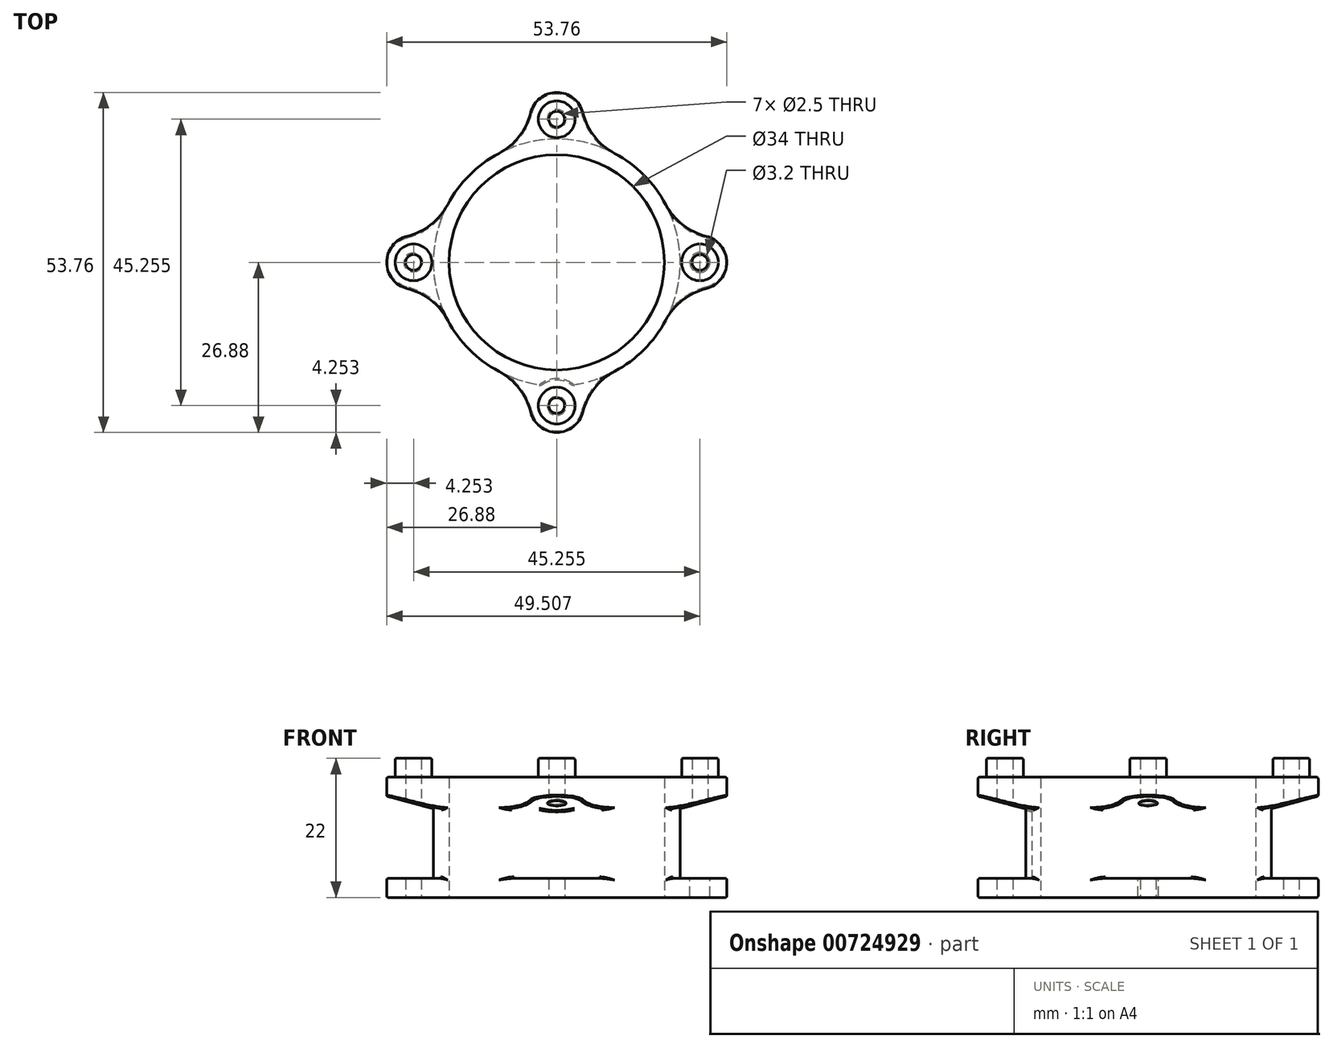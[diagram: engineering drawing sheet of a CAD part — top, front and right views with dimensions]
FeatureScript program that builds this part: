
annotation { "Feature Type Name" : "Feature", "Feature Type Description" : "" }
export const myFeature = defineFeature(function(context is Context, id is Id, definition is map)
    precondition{}
    {
        {
            var Q0;
            Q0=qCreatedBy(makeId("Top.planeOp"),FACE);
            var sketch = newSketch(context, id + "F0", { "sketchPlane" : qUnion([Q0])});
            skCircle(sketch, "E0", {"center": v(0, 0) * mm, "radius": 17 * mm});
            skArc(sketch, "E1", {"start": v(17.22, 9.14) * mm, "mid": v(13.79, 13.79) * mm, "end": v(9.14, 17.22) * mm});
            skCircle(sketch, "E2", {"center": v(22.63, 0) * mm, "radius": 1.25 * mm});
            skLineSegment(sketch, "E3.bottom", {"start": v(0, 0) * mm, "end": v(22.63, 0) * mm, "construction": true});
            skLineSegment(sketch, "E3.top", {"start": v(0, -22.63) * mm, "end": v(22.63, -22.63) * mm, "construction": true});
            skLineSegment(sketch, "E3.left", {"start": v(0, 0) * mm, "end": v(0, -22.63) * mm, "construction": true});
            skLineSegment(sketch, "E3.right", {"start": v(22.63, 0) * mm, "end": v(22.63, -22.63) * mm, "construction": true});
            skArc(sketch, "E4", {"start": v(23.65, -4.13) * mm, "mid": v(26.88, 0) * mm, "end": v(23.65, 4.13) * mm});
            skPoint(sketch, "E5.visualSharp", {"position": v(19.32, 2.67) * mm});
            skArc(sketch, "E5.filletArc", {"start": v(17.22, 9.14) * mm, "mid": v(19.9, 5.95) * mm, "end": v(23.65, 4.13) * mm});
            skPoint(sketch, "E6.visualSharp", {"position": v(19.32, -2.67) * mm});
            skArc(sketch, "E6.filletArc", {"start": v(23.65, -4.13) * mm, "mid": v(19.9, -5.95) * mm, "end": v(17.22, -9.14) * mm});
            skArc(sketch, "E7.1.0", {"start": v(-9.14, 17.22) * mm, "mid": v(-5.95, 19.9) * mm, "end": v(-4.13, 23.65) * mm});
            skArc(sketch, "E7.1.1", {"start": v(4.13, 23.65) * mm, "mid": v(0, 26.88) * mm, "end": v(-4.13, 23.65) * mm});
            skArc(sketch, "E7.1.2", {"start": v(4.13, 23.65) * mm, "mid": v(5.95, 19.9) * mm, "end": v(9.14, 17.22) * mm});
            skCircle(sketch, "E7.1.3", {"center": v(0, 22.63) * mm, "radius": 1.25 * mm});
            skArc(sketch, "E7.2.0", {"start": v(-17.22, -9.14) * mm, "mid": v(-19.9, -5.95) * mm, "end": v(-23.65, -4.13) * mm});
            skArc(sketch, "E7.2.1", {"start": v(-23.65, 4.13) * mm, "mid": v(-26.88, 0) * mm, "end": v(-23.65, -4.13) * mm});
            skArc(sketch, "E7.2.2", {"start": v(-23.65, 4.13) * mm, "mid": v(-19.9, 5.95) * mm, "end": v(-17.22, 9.14) * mm});
            skCircle(sketch, "E7.2.3", {"center": v(-22.63, 0) * mm, "radius": 1.25 * mm});
            skArc(sketch, "E8.trimOffspring", {"start": v(-9.14, 17.22) * mm, "mid": v(-13.79, 13.79) * mm, "end": v(-17.22, 9.14) * mm});
            skArc(sketch, "E9.trimOffspring", {"start": v(9.14, -17.22) * mm, "mid": v(13.79, -13.79) * mm, "end": v(17.22, -9.14) * mm});
            skArc(sketch, "E10.4.3.0", {"start": v(-4.13, -23.65) * mm, "mid": v(0, -26.88) * mm, "end": v(4.13, -23.65) * mm});
            skArc(sketch, "E10.8.3.0", {"start": v(-4.13, -23.65) * mm, "mid": v(-5.95, -19.9) * mm, "end": v(-9.14, -17.22) * mm});
            skArc(sketch, "E10.11.3.0", {"start": v(9.14, -17.22) * mm, "mid": v(5.95, -19.9) * mm, "end": v(4.13, -23.65) * mm});
            skCircle(sketch, "E10.12.3.0", {"center": v(0, -22.63) * mm, "radius": 1.25 * mm});
            skArc(sketch, "E11.trimOffspring", {"start": v(-17.22, -9.14) * mm, "mid": v(-13.79, -13.79) * mm, "end": v(-9.14, -17.22) * mm});
            skSolve(sketch);
        }
        {
            var Q0;
            Q0=makeQuery(id+"F0.imprint","IMPRINT",FACE,{"disambiguationData":[TD([[makeQuery(id+"F0.imprint","IMPRINT",EDGE,{"derivedFrom":sQuery(id+"F0.wireOp",EDGE,"E0")}),-1.0]])]});
            extrude(context, id + "F1", {"entities" : qUnion([Q0]), "depth" : 22 * mm, "offsetDistance" : 25 * mm});
        }
        {
            var Q0;
            Q0=qCreatedBy(makeId("Front.planeOp"),FACE);
            var sketch = newSketch(context, id + "F2", { "sketchPlane" : qUnion([Q0])});
            skLineSegment(sketch, "E12.bottom", {"start": v(-26.88, 16) * mm, "end": v(-19.5, 14.02) * mm});
            skLineSegment(sketch, "E12.top", {"start": v(-26.88, 3) * mm, "end": v(-19.5, 3) * mm});
            skLineSegment(sketch, "E12.left", {"start": v(-26.88, 16) * mm, "end": v(-26.88, 3) * mm});
            skLineSegment(sketch, "E12.right", {"start": v(-19.5, 14.02) * mm, "end": v(-19.5, 3) * mm});
            skLineSegment(sketch, "E13", {"start": v(-26.88, 0) * mm, "end": v(-26.88, 22) * mm});
            skLineSegment(sketch, "E14", {"start": v(-17, 0) * mm, "end": v(-17, 22) * mm, "construction": true});
            skSolve(sketch);
        }
        {
            var Q0;
            Q0 = qSketchRegion(id + "F2", true);
            var Q1;
            Q1=makeQuery(id+"F1.opExtrude","SWEPT_FACE",FACE,{"disambiguationData":[OSD([sQuery(id+"F0.wireOp",EDGE,"E0")])]});
            revolve(context, id + "F3", {"operationType" : NewBodyOperationType.REMOVE, "surfaceOperationType" : NewSurfaceOperationType.NEW, "entities" : qUnion([Q0]), "axis" : qUnion([Q1]), "revolveType" : RevolveType.FULL, "oppositeDirection" : true});
        }
        {
            var Q0;
            Q0=makeQuery(id+"F3.boolean.opBoolean","COPY",FACE,{"disambiguationData":[TD([makeQuery(id+"F1.opExtrude","SWEPT_FACE",FACE,{"disambiguationData":[OSD([sQuery(id+"F0.wireOp",EDGE,"E10.4.3.0")])]})])],"derivedFrom":makeQuery(id+"F3.opRevolve","SWEPT_FACE",FACE,{"disambiguationData":[OSD([sQuery(id+"F2.wireOp",EDGE,"E12.top")])]})});
            var sketch = newSketch(context, id + "F4", { "sketchPlane" : qUnion([Q0])});
            skCircle(sketch, "E15", {"center": v(0, -22.63) * mm, "radius": 4.25 * mm});
            skSolve(sketch);
        }
        {
            var Q0;
            Q0 = qSketchRegion(id + "F4", true);
            var Q1;
            Q1=makeQuery(id+"F3.boolean.opBoolean","COPY",FACE,{"disambiguationData":[TD([makeQuery(id+"F1.opExtrude","SWEPT_FACE",FACE,{"disambiguationData":[OSD([sQuery(id+"F0.wireOp",EDGE,"E10.4.3.0")])]})])],"derivedFrom":makeQuery(id+"F3.opRevolve","SWEPT_FACE",FACE,{"disambiguationData":[OSD([sQuery(id+"F2.wireOp",EDGE,"E12.bottom")])]})});
            extrude(context, id + "F5", {"entities" : qUnion([Q0]), "operationType" : NewBodyOperationType.REMOVE, "endBound" : BoundingType.UP_TO_SURFACE, "depth" : 10 * mm, "endBoundEntityFace" : qUnion([Q1]), "offsetDistance" : 25 * mm});
        }
        {
            var Q0;
            Q0=makeQuery(id+"F1.opExtrude","CAP_FACE",FACE,{"disambiguationData":[OSD([sQuery(id+"F0.wireOp",EDGE,"E0"),sQuery(id+"F0.wireOp",EDGE,"E1"),sQuery(id+"F0.wireOp",EDGE,"E2"),sQuery(id+"F0.wireOp",EDGE,"E4"),sQuery(id+"F0.wireOp",EDGE,"E5.filletArc"),sQuery(id+"F0.wireOp",EDGE,"E6.filletArc"),sQuery(id+"F0.wireOp",EDGE,"E7.1.0"),sQuery(id+"F0.wireOp",EDGE,"E7.1.1"),sQuery(id+"F0.wireOp",EDGE,"E7.1.2"),sQuery(id+"F0.wireOp",EDGE,"E7.1.3"),sQuery(id+"F0.wireOp",EDGE,"E7.2.0"),sQuery(id+"F0.wireOp",EDGE,"E7.2.1"),sQuery(id+"F0.wireOp",EDGE,"E7.2.2"),sQuery(id+"F0.wireOp",EDGE,"E7.2.3"),sQuery(id+"F0.wireOp",EDGE,"E8.trimOffspring"),sQuery(id+"F0.wireOp",EDGE,"E9.trimOffspring"),sQuery(id+"F0.wireOp",EDGE,"E10.4.3.0"),sQuery(id+"F0.wireOp",EDGE,"E10.8.3.0"),sQuery(id+"F0.wireOp",EDGE,"E10.11.3.0"),sQuery(id+"F0.wireOp",EDGE,"E10.12.3.0"),sQuery(id+"F0.wireOp",EDGE,"E11.trimOffspring")])],"isStart":false});
            var sketch = newSketch(context, id + "F6", { "sketchPlane" : qUnion([Q0])});
            skCircle(sketch, "E16", {"center": v(22.63, 0) * mm, "radius": 2.9 * mm});
            skCircle(sketch, "E17.1.0", {"center": v(0, 22.63) * mm, "radius": 2.9 * mm});
            skCircle(sketch, "E17.2.0", {"center": v(-22.63, 0) * mm, "radius": 2.9 * mm});
            skCircle(sketch, "E17.3.0", {"center": v(0, -22.63) * mm, "radius": 2.9 * mm});
            skPoint(sketch, "E17.center", {"position": v(0, 0) * mm});
            skCircle(sketch, "E18", {"center": v(0, 0) * mm, "radius": 46.42 * mm});
            skSolve(sketch);
        }
        {
            var Q0;
            Q0 = qSketchRegion(id + "F6", true);
            extrude(context, id + "F7", {"entities" : qUnion([Q0]), "operationType" : NewBodyOperationType.REMOVE, "oppositeDirection" : true, "depth" : 3 * mm, "offsetDistance" : 25 * mm});
        }
        {
            var Q0;
            Q0=makeQuery(id+"FENhaPdsYRhXpVq_1.1.F5.boolean.opBoolean","MERGE",FACE,{"derivedFrom":[makeQuery(id+"F3.boolean.opBoolean","COPY",FACE,{"disambiguationData":[TD([makeQuery(id+"F1.opExtrude","SWEPT_FACE",FACE,{"disambiguationData":[OSD([sQuery(id+"F0.wireOp",EDGE,"E2")])]})])],"derivedFrom":makeQuery(id+"F3.opRevolve","SWEPT_FACE",FACE,{"disambiguationData":[OSD([sQuery(id+"F2.wireOp",EDGE,"E12.top")])]})}),makeQuery(id+"FENhaPdsYRhXpVq_1.1.F5.opExtrude","CAP_FACE",FACE,{"disambiguationData":[OSD([sQuery(id+"F4.wireOp",EDGE,"E15")])],"isStart":true})]});
            var sketch = newSketch(context, id + "F8", { "sketchPlane" : qUnion([Q0])});
            skPoint(sketch, "E19", {"position": v(22.63, 0) * mm});
            skSolve(sketch);
        }
        {
            var Q0;
            Q0=sQuery(id+"F8.wireOp",VERTEX,"E19");
            var Q1;
            Q1=makeQuery(id+"F1.opExtrude","SWEPT_BODY",BODY,{"disambiguationData":[OSD([sQuery(id+"F0.wireOp",EDGE,"E0"),sQuery(id+"F0.wireOp",EDGE,"E1"),sQuery(id+"F0.wireOp",EDGE,"E2"),sQuery(id+"F0.wireOp",EDGE,"E4"),sQuery(id+"F0.wireOp",EDGE,"E5.filletArc"),sQuery(id+"F0.wireOp",EDGE,"E6.filletArc"),sQuery(id+"F0.wireOp",EDGE,"E7.1.0"),sQuery(id+"F0.wireOp",EDGE,"E7.1.1"),sQuery(id+"F0.wireOp",EDGE,"E7.1.2"),sQuery(id+"F0.wireOp",EDGE,"E7.1.3"),sQuery(id+"F0.wireOp",EDGE,"E7.2.0"),sQuery(id+"F0.wireOp",EDGE,"E7.2.1"),sQuery(id+"F0.wireOp",EDGE,"E7.2.2"),sQuery(id+"F0.wireOp",EDGE,"E7.2.3"),sQuery(id+"F0.wireOp",EDGE,"E8.trimOffspring"),sQuery(id+"F0.wireOp",EDGE,"E9.trimOffspring"),sQuery(id+"F0.wireOp",EDGE,"E10.4.3.0"),sQuery(id+"F0.wireOp",EDGE,"E10.8.3.0"),sQuery(id+"F0.wireOp",EDGE,"E10.11.3.0"),sQuery(id+"F0.wireOp",EDGE,"E10.12.3.0"),sQuery(id+"F0.wireOp",EDGE,"E11.trimOffspring")])]});
            hole(context, id + "F9", {"style" : HoleStyle.SIMPLE, "endStyle" : HoleEndStyle.THROUGH, "holeDiameter" : 3.2 * mm, "majorDiameter" : 5 * mm, "isTappedThrough" : true, "tappedDepth" : 12 * mm, "tapClearance" : 3, "locations" : qUnion([Q0]), "scope" : qUnion([Q1])});
        }
        {
            var Q0;
            Q0=makeQuery(id+"F1.opExtrude","CAP_EDGE",EDGE,{"disambiguationData":[OSD([sQuery(id+"F0.wireOp",EDGE,"E7.2.0")])],"isStart":true});
            var Q1;
            {var subQ1=sQuery(id+"F0.wireOp",EDGE,"E9.trimOffspring");var subQ2=makeQuery(id+"F1.opExtrude","SWEPT_FACE",FACE,{"disambiguationData":[OSD([subQ1])]});var subQ3=sQuery(id+"F0.wireOp",EDGE,"E8.trimOffspring");var subQ4=makeQuery(id+"F1.opExtrude","SWEPT_FACE",FACE,{"disambiguationData":[OSD([subQ3])]});var subQ7=sQuery(id+"F0.wireOp",EDGE,"E1");var subQ8=makeQuery(id+"F1.opExtrude","SWEPT_FACE",FACE,{"disambiguationData":[OSD([subQ7])]});var subQ9=makeQuery(id+"F3.opRevolve","SWEPT_FACE",FACE,{"disambiguationData":[OSD([sQuery(id+"F2.wireOp",EDGE,"E12.right")])]});var subQ16=sQuery(id+"F0.wireOp",EDGE,"E11.trimOffspring");var subQ17=makeQuery(id+"F1.opExtrude","SWEPT_FACE",FACE,{"disambiguationData":[OSD([subQ16])]});var subQ25=sQuery(id+"F0.wireOp",EDGE,"E6.filletArc");var subQ26=makeQuery(id+"F1.opExtrude","SWEPT_FACE",FACE,{"disambiguationData":[OSD([subQ25])]});Q1=makeQuery(id+"FENhaPdsYRhXpVq_1.1.F5.boolean.opBoolean","SPLIT",FACE,{"disambiguationData":[TD([subQ26])],"derivedFrom":makeQuery(id+"F3.boolean.opBoolean","MERGE",FACE,{"derivedFrom":[subQ8,subQ4,subQ2,subQ17,subQ9]})});}
            var Q2;
            Q2=makeQuery(id+"F1.opExtrude","CAP_EDGE",EDGE,{"disambiguationData":[OSD([sQuery(id+"F0.wireOp",EDGE,"E0")])],"isStart":false});
            var Q3;
            Q3=makeQuery(id+"F1.opExtrude","CAP_EDGE",EDGE,{"disambiguationData":[OSD([sQuery(id+"F0.wireOp",EDGE,"E10.11.3.0")])],"isStart":true});
            var Q4;
            Q4=makeQuery(id+"F3.boolean.opBoolean","INTERSECT",EDGE,{"derivedFrom":[makeQuery(id+"F1.opExtrude","SWEPT_FACE",FACE,{"disambiguationData":[OSD([sQuery(id+"F0.wireOp",EDGE,"E10.4.3.0")])]}),makeQuery(id+"F3.opRevolve","SWEPT_FACE",FACE,{"disambiguationData":[OSD([sQuery(id+"F2.wireOp",EDGE,"E12.top")])]})]});
            var Q5;
            Q5=makeQuery(id+"F1.opExtrude","CAP_EDGE",EDGE,{"disambiguationData":[OSD([sQuery(id+"F0.wireOp",EDGE,"E7.2.1")])],"isStart":true});
            var Q6;
            {var subQ1=sQuery(id+"F0.wireOp",EDGE,"E7.2.1");Q6=makeQuery(id+"F3.boolean.opBoolean","SPLIT",FACE,{"disambiguationData":[TD([makeQuery(id+"F3.opRevolve","SWEPT_FACE",FACE,{"disambiguationData":[OSD([sQuery(id+"F2.wireOp",EDGE,"E12.top")])]})])],"derivedFrom":makeQuery(id+"F1.opExtrude","SWEPT_FACE",FACE,{"disambiguationData":[OSD([subQ1])]})});}
            var Q7;
            Q7=makeQuery(id+"F3.boolean.opBoolean","INTERSECT",EDGE,{"derivedFrom":[makeQuery(id+"F1.opExtrude","SWEPT_FACE",FACE,{"disambiguationData":[OSD([sQuery(id+"F0.wireOp",EDGE,"E2")])]}),makeQuery(id+"F3.opRevolve","SWEPT_FACE",FACE,{"disambiguationData":[OSD([sQuery(id+"F2.wireOp",EDGE,"E12.top")])]})]});
            var Q8;
            Q8=makeQuery(id+"F1.opExtrude","CAP_EDGE",EDGE,{"disambiguationData":[OSD([sQuery(id+"F0.wireOp",EDGE,"E11.trimOffspring")])],"isStart":false});
            var Q9;
            {var subQ0=sQuery(id+"F0.wireOp",EDGE,"E2");Q9=makeQuery(id+"F3.boolean.opBoolean","SPLIT",FACE,{"disambiguationData":[TD([makeQuery(id+"F3.opRevolve","SWEPT_FACE",FACE,{"disambiguationData":[OSD([sQuery(id+"F2.wireOp",EDGE,"E12.top")])]})])],"derivedFrom":makeQuery(id+"F1.opExtrude","SWEPT_FACE",FACE,{"disambiguationData":[OSD([subQ0])]})});}
            var Q10;
            Q10=makeQuery(id+"F1.opExtrude","CAP_EDGE",EDGE,{"disambiguationData":[OSD([sQuery(id+"F0.wireOp",EDGE,"E7.1.0")])],"isStart":false});
            var Q11;
            Q11=makeQuery(id+"F1.opExtrude","CAP_EDGE",EDGE,{"disambiguationData":[OSD([sQuery(id+"F0.wireOp",EDGE,"E7.2.1")])],"isStart":false});
            var Q12;
            {var subQ0=sQuery(id+"F0.wireOp",EDGE,"E10.12.3.0");Q12=makeQuery(id+"F3.boolean.opBoolean","SPLIT",FACE,{"disambiguationData":[TD([makeQuery(id+"F3.opRevolve","SWEPT_FACE",FACE,{"disambiguationData":[OSD([sQuery(id+"F2.wireOp",EDGE,"E12.top")])]})])],"derivedFrom":makeQuery(id+"F1.opExtrude","SWEPT_FACE",FACE,{"disambiguationData":[OSD([subQ0])]})});}
            var Q13;
            Q13=makeQuery(id+"F1.opExtrude","CAP_EDGE",EDGE,{"disambiguationData":[OSD([sQuery(id+"F0.wireOp",EDGE,"E10.4.3.0")])],"isStart":false});
            var Q14;
            Q14=makeQuery(id+"F1.opExtrude","CAP_FACE",FACE,{"disambiguationData":[OSD([sQuery(id+"F0.wireOp",EDGE,"E0"),sQuery(id+"F0.wireOp",EDGE,"E1"),sQuery(id+"F0.wireOp",EDGE,"E2"),sQuery(id+"F0.wireOp",EDGE,"E4"),sQuery(id+"F0.wireOp",EDGE,"E5.filletArc"),sQuery(id+"F0.wireOp",EDGE,"E6.filletArc"),sQuery(id+"F0.wireOp",EDGE,"E7.1.0"),sQuery(id+"F0.wireOp",EDGE,"E7.1.1"),sQuery(id+"F0.wireOp",EDGE,"E7.1.2"),sQuery(id+"F0.wireOp",EDGE,"E7.1.3"),sQuery(id+"F0.wireOp",EDGE,"E7.2.0"),sQuery(id+"F0.wireOp",EDGE,"E7.2.1"),sQuery(id+"F0.wireOp",EDGE,"E7.2.2"),sQuery(id+"F0.wireOp",EDGE,"E7.2.3"),sQuery(id+"F0.wireOp",EDGE,"E8.trimOffspring"),sQuery(id+"F0.wireOp",EDGE,"E9.trimOffspring"),sQuery(id+"F0.wireOp",EDGE,"E10.4.3.0"),sQuery(id+"F0.wireOp",EDGE,"E10.8.3.0"),sQuery(id+"F0.wireOp",EDGE,"E10.11.3.0"),sQuery(id+"F0.wireOp",EDGE,"E10.12.3.0"),sQuery(id+"F0.wireOp",EDGE,"E11.trimOffspring")])],"isStart":false});
            var Q15;
            Q15=makeQuery(id+"F1.opExtrude","CAP_EDGE",EDGE,{"disambiguationData":[OSD([sQuery(id+"F0.wireOp",EDGE,"E10.8.3.0")])],"isStart":true});
            var Q16;
            Q16=makeQuery(id+"F3.boolean.opBoolean","INTERSECT",EDGE,{"derivedFrom":[makeQuery(id+"F1.opExtrude","SWEPT_FACE",FACE,{"disambiguationData":[OSD([sQuery(id+"F0.wireOp",EDGE,"E7.2.1")])]}),makeQuery(id+"F3.opRevolve","SWEPT_FACE",FACE,{"disambiguationData":[OSD([sQuery(id+"F2.wireOp",EDGE,"E12.bottom")])]})]});
            var Q17;
            Q17=makeQuery(id+"F3.boolean.opBoolean","INTERSECT",EDGE,{"derivedFrom":[makeQuery(id+"F1.opExtrude","SWEPT_FACE",FACE,{"disambiguationData":[OSD([sQuery(id+"F0.wireOp",EDGE,"E10.4.3.0")])]}),makeQuery(id+"F3.opRevolve","SWEPT_FACE",FACE,{"disambiguationData":[OSD([sQuery(id+"F2.wireOp",EDGE,"E12.bottom")])]})]});
            var Q18;
            Q18=makeQuery(id+"F3.boolean.opBoolean","INTERSECT",EDGE,{"derivedFrom":[makeQuery(id+"F1.opExtrude","SWEPT_FACE",FACE,{"disambiguationData":[OSD([sQuery(id+"F0.wireOp",EDGE,"E10.11.3.0")])]}),makeQuery(id+"F3.opRevolve","SWEPT_FACE",FACE,{"disambiguationData":[OSD([sQuery(id+"F2.wireOp",EDGE,"E12.bottom")])]})]});
            var Q19;
            Q19=makeQuery(id+"F1.opExtrude","CAP_EDGE",EDGE,{"disambiguationData":[OSD([sQuery(id+"F0.wireOp",EDGE,"E9.trimOffspring")])],"isStart":true});
            var Q20;
            {var subQ4=sQuery(id+"F0.wireOp",EDGE,"E10.11.3.0");Q20=makeQuery(id+"F3.boolean.opBoolean","SPLIT",FACE,{"disambiguationData":[TD([makeQuery(id+"F3.opRevolve","SWEPT_FACE",FACE,{"disambiguationData":[OSD([sQuery(id+"F2.wireOp",EDGE,"E12.bottom")])]})])],"derivedFrom":makeQuery(id+"F1.opExtrude","SWEPT_FACE",FACE,{"disambiguationData":[OSD([subQ4])]})});}
            var Q21;
            Q21=makeQuery(id+"F1.opExtrude","CAP_EDGE",EDGE,{"disambiguationData":[OSD([sQuery(id+"F0.wireOp",EDGE,"E8.trimOffspring")])],"isStart":false});
            var Q22;
            Q22=makeQuery(id+"F1.opExtrude","CAP_EDGE",EDGE,{"disambiguationData":[OSD([sQuery(id+"F0.wireOp",EDGE,"E6.filletArc")])],"isStart":false});
            var Q23;
            Q23=makeQuery(id+"FENhaPdsYRhXpVq_1.3.F5.boolean.opBoolean","MERGE",FACE,{"derivedFrom":[makeQuery(id+"F3.boolean.opBoolean","COPY",FACE,{"disambiguationData":[TD([makeQuery(id+"F1.opExtrude","SWEPT_FACE",FACE,{"disambiguationData":[OSD([sQuery(id+"F0.wireOp",EDGE,"E7.2.0")])]})])],"derivedFrom":makeQuery(id+"F3.opRevolve","SWEPT_FACE",FACE,{"disambiguationData":[OSD([sQuery(id+"F2.wireOp",EDGE,"E12.top")])]})}),makeQuery(id+"FENhaPdsYRhXpVq_1.3.F5.opExtrude","CAP_FACE",FACE,{"disambiguationData":[OSD([sQuery(id+"F4.wireOp",EDGE,"E15")])],"isStart":true})]});
            var Q24;
            {var subQ0=makeQuery(id+"F1.opExtrude","SWEPT_FACE",FACE,{"disambiguationData":[OSD([sQuery(id+"F0.wireOp",EDGE,"E10.8.3.0")])]});var subQ5=sQuery(id+"F2.wireOp",EDGE,"E12.right");var subQ9=sQuery(id+"F2.wireOp",EDGE,"E12.top");Q24=makeQuery(id+"F5.boolean.opBoolean","SPLIT",EDGE,{"disambiguationData":[TD([subQ0])],"derivedFrom":makeQuery(id+"F3.boolean.opBoolean","COPY",EDGE,{"disambiguationData":[TD([subQ0])],"derivedFrom":makeQuery(id+"F3.opRevolve","SWEPT_EDGE",EDGE,{"disambiguationData":[OSD([subQ9,subQ5])]})})});}
            var Q25;
            Q25=makeQuery(id+"F1.opExtrude","CAP_EDGE",EDGE,{"disambiguationData":[OSD([sQuery(id+"F0.wireOp",EDGE,"E5.filletArc")])],"isStart":false});
            var Q26;
            {var subQ2=makeQuery(id+"F1.opExtrude","SWEPT_FACE",FACE,{"disambiguationData":[OSD([sQuery(id+"F0.wireOp",EDGE,"E6.filletArc")])]});var subQ4=sQuery(id+"F2.wireOp",EDGE,"E12.right");var subQ8=makeQuery(id+"F1.opExtrude","SWEPT_FACE",FACE,{"disambiguationData":[OSD([sQuery(id+"F0.wireOp",EDGE,"E5.filletArc")])]});var subQ9=sQuery(id+"F2.wireOp",EDGE,"E12.top");Q26=makeQuery(id+"FENhaPdsYRhXpVq_1.1.F5.boolean.opBoolean","SPLIT",EDGE,{"disambiguationData":[TD([subQ2])],"derivedFrom":makeQuery(id+"F3.boolean.opBoolean","COPY",EDGE,{"disambiguationData":[TD([subQ8])],"derivedFrom":makeQuery(id+"F3.opRevolve","SWEPT_EDGE",EDGE,{"disambiguationData":[OSD([subQ9,subQ4])]})})});}
            var Q27;
            Q27=makeQuery(id+"F1.opExtrude","CAP_EDGE",EDGE,{"disambiguationData":[OSD([sQuery(id+"F0.wireOp",EDGE,"E7.1.3")])],"isStart":false});
            var Q28;
            Q28=makeQuery(id+"F3.boolean.opBoolean","INTERSECT",EDGE,{"derivedFrom":[makeQuery(id+"F1.opExtrude","SWEPT_FACE",FACE,{"disambiguationData":[OSD([sQuery(id+"F0.wireOp",EDGE,"E10.8.3.0")])]}),makeQuery(id+"F3.opRevolve","SWEPT_FACE",FACE,{"disambiguationData":[OSD([sQuery(id+"F2.wireOp",EDGE,"E12.bottom")])]})]});
            var Q29;
            {var subQ4=sQuery(id+"F0.wireOp",EDGE,"E10.11.3.0");Q29=makeQuery(id+"F3.boolean.opBoolean","SPLIT",FACE,{"disambiguationData":[TD([makeQuery(id+"F3.opRevolve","SWEPT_FACE",FACE,{"disambiguationData":[OSD([sQuery(id+"F2.wireOp",EDGE,"E12.top")])]})])],"derivedFrom":makeQuery(id+"F1.opExtrude","SWEPT_FACE",FACE,{"disambiguationData":[OSD([subQ4])]})});}
            var Q30;
            {var subQ0=sQuery(id+"F0.wireOp",EDGE,"E7.2.3");Q30=makeQuery(id+"F3.boolean.opBoolean","SPLIT",FACE,{"disambiguationData":[TD([makeQuery(id+"F3.opRevolve","SWEPT_FACE",FACE,{"disambiguationData":[OSD([sQuery(id+"F2.wireOp",EDGE,"E12.top")])]})])],"derivedFrom":makeQuery(id+"F1.opExtrude","SWEPT_FACE",FACE,{"disambiguationData":[OSD([subQ0])]})});}
            var Q31;
            {var subQ0=sQuery(id+"F0.wireOp",EDGE,"E2");Q31=makeQuery(id+"F3.boolean.opBoolean","SPLIT",FACE,{"disambiguationData":[TD([makeQuery(id+"F3.opRevolve","SWEPT_FACE",FACE,{"disambiguationData":[OSD([sQuery(id+"F2.wireOp",EDGE,"E12.bottom")])]})])],"derivedFrom":makeQuery(id+"F1.opExtrude","SWEPT_FACE",FACE,{"disambiguationData":[OSD([subQ0])]})});}
            var Q32;
            {var subQ5=sQuery(id+"F0.wireOp",EDGE,"E7.1.2");Q32=makeQuery(id+"F3.boolean.opBoolean","SPLIT",FACE,{"disambiguationData":[TD([makeQuery(id+"F3.opRevolve","SWEPT_FACE",FACE,{"disambiguationData":[OSD([sQuery(id+"F2.wireOp",EDGE,"E12.bottom")])]})])],"derivedFrom":makeQuery(id+"F1.opExtrude","SWEPT_FACE",FACE,{"disambiguationData":[OSD([subQ5])]})});}
            var Q33;
            Q33=makeQuery(id+"F3.boolean.opBoolean","INTERSECT",EDGE,{"derivedFrom":[makeQuery(id+"F1.opExtrude","SWEPT_FACE",FACE,{"disambiguationData":[OSD([sQuery(id+"F0.wireOp",EDGE,"E4")])]}),makeQuery(id+"F3.opRevolve","SWEPT_FACE",FACE,{"disambiguationData":[OSD([sQuery(id+"F2.wireOp",EDGE,"E12.bottom")])]})]});
            var Q34;
            {var subQ1=sQuery(id+"F0.wireOp",EDGE,"E7.2.1");Q34=makeQuery(id+"F3.boolean.opBoolean","SPLIT",FACE,{"disambiguationData":[TD([makeQuery(id+"F3.opRevolve","SWEPT_FACE",FACE,{"disambiguationData":[OSD([sQuery(id+"F2.wireOp",EDGE,"E12.bottom")])]})])],"derivedFrom":makeQuery(id+"F1.opExtrude","SWEPT_FACE",FACE,{"disambiguationData":[OSD([subQ1])]})});}
            var Q35;
            {var subQ5=sQuery(id+"F0.wireOp",EDGE,"E7.2.0");Q35=makeQuery(id+"F3.boolean.opBoolean","SPLIT",FACE,{"disambiguationData":[TD([makeQuery(id+"F3.opRevolve","SWEPT_FACE",FACE,{"disambiguationData":[OSD([sQuery(id+"F2.wireOp",EDGE,"E12.top")])]})])],"derivedFrom":makeQuery(id+"F1.opExtrude","SWEPT_FACE",FACE,{"disambiguationData":[OSD([subQ5])]})});}
            var Q36;
            Q36=makeQuery(id+"F1.opExtrude","CAP_EDGE",EDGE,{"disambiguationData":[OSD([sQuery(id+"F0.wireOp",EDGE,"E10.4.3.0")])],"isStart":true});
            var Q37;
            Q37=makeQuery(id+"F5.boolean.opBoolean","COPY",FACE,{"derivedFrom":makeQuery(id+"F5.opExtrude","SWEPT_FACE",FACE,{"disambiguationData":[OSD([sQuery(id+"F4.wireOp",EDGE,"E15")])]})});
            var Q38;
            Q38=makeQuery(id+"F1.opExtrude","CAP_EDGE",EDGE,{"disambiguationData":[OSD([sQuery(id+"F0.wireOp",EDGE,"E7.2.2")])],"isStart":false});
            var Q39;
            Q39=makeQuery(id+"F1.opExtrude","CAP_EDGE",EDGE,{"disambiguationData":[OSD([sQuery(id+"F0.wireOp",EDGE,"E7.2.0")])],"isStart":false});
            var Q40;
            {var subQ2=sQuery(id+"F0.wireOp",EDGE,"E1");var subQ3=makeQuery(id+"F1.opExtrude","SWEPT_FACE",FACE,{"disambiguationData":[OSD([subQ2])]});var subQ4=makeQuery(id+"F3.opRevolve","SWEPT_FACE",FACE,{"disambiguationData":[OSD([sQuery(id+"F2.wireOp",EDGE,"E12.right")])]});var subQ11=sQuery(id+"F0.wireOp",EDGE,"E8.trimOffspring");var subQ12=makeQuery(id+"F1.opExtrude","SWEPT_FACE",FACE,{"disambiguationData":[OSD([subQ11])]});var subQ13=sQuery(id+"F0.wireOp",EDGE,"E9.trimOffspring");var subQ14=makeQuery(id+"F1.opExtrude","SWEPT_FACE",FACE,{"disambiguationData":[OSD([subQ13])]});var subQ15=sQuery(id+"F0.wireOp",EDGE,"E11.trimOffspring");var subQ16=makeQuery(id+"F1.opExtrude","SWEPT_FACE",FACE,{"disambiguationData":[OSD([subQ15])]});var subQ23=sQuery(id+"F0.wireOp",EDGE,"E7.1.0");var subQ24=makeQuery(id+"F1.opExtrude","SWEPT_FACE",FACE,{"disambiguationData":[OSD([subQ23])]});var subQ35=sQuery(id+"F0.wireOp",EDGE,"E5.filletArc");var subQ55=makeQuery(id+"F1.opExtrude","SWEPT_FACE",FACE,{"disambiguationData":[OSD([subQ35])]});Q40=makeQuery(id+"FENhaPdsYRhXpVq_1.3.F5.boolean.opBoolean","SPLIT",FACE,{"disambiguationData":[TD([subQ24])],"derivedFrom":makeQuery(id+"FENhaPdsYRhXpVq_1.2.F5.boolean.opBoolean","SPLIT",FACE,{"disambiguationData":[TD([subQ24])],"derivedFrom":makeQuery(id+"FENhaPdsYRhXpVq_1.1.F5.boolean.opBoolean","SPLIT",FACE,{"disambiguationData":[TD([subQ55])],"derivedFrom":makeQuery(id+"F3.boolean.opBoolean","MERGE",FACE,{"derivedFrom":[subQ3,subQ12,subQ14,subQ16,subQ4]})})})});}
            var Q41;
            Q41=makeQuery(id+"FENhaPdsYRhXpVq_1.1.F5.boolean.opBoolean","MERGE",FACE,{"derivedFrom":[makeQuery(id+"F3.boolean.opBoolean","COPY",FACE,{"disambiguationData":[TD([makeQuery(id+"F1.opExtrude","SWEPT_FACE",FACE,{"disambiguationData":[OSD([sQuery(id+"F0.wireOp",EDGE,"E2")])]})])],"derivedFrom":makeQuery(id+"F3.opRevolve","SWEPT_FACE",FACE,{"disambiguationData":[OSD([sQuery(id+"F2.wireOp",EDGE,"E12.top")])]})}),makeQuery(id+"FENhaPdsYRhXpVq_1.1.F5.opExtrude","CAP_FACE",FACE,{"disambiguationData":[OSD([sQuery(id+"F4.wireOp",EDGE,"E15")])],"isStart":true})]});
            var Q42;
            Q42=makeQuery(id+"F3.boolean.opBoolean","INTERSECT",EDGE,{"derivedFrom":[makeQuery(id+"F1.opExtrude","SWEPT_FACE",FACE,{"disambiguationData":[OSD([sQuery(id+"F0.wireOp",EDGE,"E7.2.0")])]}),makeQuery(id+"F3.opRevolve","SWEPT_FACE",FACE,{"disambiguationData":[OSD([sQuery(id+"F2.wireOp",EDGE,"E12.top")])]})]});
            var Q43;
            Q43=makeQuery(id+"F1.opExtrude","CAP_EDGE",EDGE,{"disambiguationData":[OSD([sQuery(id+"F0.wireOp",EDGE,"E10.11.3.0")])],"isStart":false});
            var Q44;
            {var subQ4=sQuery(id+"F0.wireOp",EDGE,"E7.2.2");Q44=makeQuery(id+"F3.boolean.opBoolean","SPLIT",FACE,{"disambiguationData":[TD([makeQuery(id+"F3.opRevolve","SWEPT_FACE",FACE,{"disambiguationData":[OSD([sQuery(id+"F2.wireOp",EDGE,"E12.bottom")])]})])],"derivedFrom":makeQuery(id+"F1.opExtrude","SWEPT_FACE",FACE,{"disambiguationData":[OSD([subQ4])]})});}
            var Q45;
            Q45=makeQuery(id+"F1.opExtrude","CAP_EDGE",EDGE,{"disambiguationData":[OSD([sQuery(id+"F0.wireOp",EDGE,"E4")])],"isStart":true});
            var Q46;
            {var subQ1=sQuery(id+"F0.wireOp",EDGE,"E7.1.1");Q46=makeQuery(id+"F3.boolean.opBoolean","SPLIT",FACE,{"disambiguationData":[TD([makeQuery(id+"F3.opRevolve","SWEPT_FACE",FACE,{"disambiguationData":[OSD([sQuery(id+"F2.wireOp",EDGE,"E12.bottom")])]})])],"derivedFrom":makeQuery(id+"F1.opExtrude","SWEPT_FACE",FACE,{"disambiguationData":[OSD([subQ1])]})});}
            var Q47;
            Q47=makeQuery(id+"F1.opExtrude","CAP_EDGE",EDGE,{"disambiguationData":[OSD([sQuery(id+"F0.wireOp",EDGE,"E6.filletArc")])],"isStart":true});
            var Q48;
            Q48=makeQuery(id+"F1.opExtrude","CAP_EDGE",EDGE,{"disambiguationData":[OSD([sQuery(id+"F0.wireOp",EDGE,"E10.12.3.0")])],"isStart":false});
            var Q49;
            Q49=makeQuery(id+"F1.opExtrude","CAP_EDGE",EDGE,{"disambiguationData":[OSD([sQuery(id+"F0.wireOp",EDGE,"E2")])],"isStart":false});
            var Q50;
            {var subQ4=sQuery(id+"F0.wireOp",EDGE,"E10.8.3.0");Q50=makeQuery(id+"F3.boolean.opBoolean","SPLIT",FACE,{"disambiguationData":[TD([makeQuery(id+"F3.opRevolve","SWEPT_FACE",FACE,{"disambiguationData":[OSD([sQuery(id+"F2.wireOp",EDGE,"E12.top")])]})])],"derivedFrom":makeQuery(id+"F1.opExtrude","SWEPT_FACE",FACE,{"disambiguationData":[OSD([subQ4])]})});}
            var Q51;
            Q51=makeQuery(id+"F1.opExtrude","CAP_EDGE",EDGE,{"disambiguationData":[OSD([sQuery(id+"F0.wireOp",EDGE,"E7.1.1")])],"isStart":false});
            var Q52;
            Q52=makeQuery(id+"F3.boolean.opBoolean","INTERSECT",EDGE,{"derivedFrom":[makeQuery(id+"F1.opExtrude","SWEPT_FACE",FACE,{"disambiguationData":[OSD([sQuery(id+"F0.wireOp",EDGE,"E7.2.1")])]}),makeQuery(id+"F3.opRevolve","SWEPT_FACE",FACE,{"disambiguationData":[OSD([sQuery(id+"F2.wireOp",EDGE,"E12.top")])]})]});
            var Q53;
            Q53=makeQuery(id+"F1.opExtrude","CAP_FACE",FACE,{"disambiguationData":[OSD([sQuery(id+"F0.wireOp",EDGE,"E0"),sQuery(id+"F0.wireOp",EDGE,"E1"),sQuery(id+"F0.wireOp",EDGE,"E2"),sQuery(id+"F0.wireOp",EDGE,"E4"),sQuery(id+"F0.wireOp",EDGE,"E5.filletArc"),sQuery(id+"F0.wireOp",EDGE,"E6.filletArc"),sQuery(id+"F0.wireOp",EDGE,"E7.1.0"),sQuery(id+"F0.wireOp",EDGE,"E7.1.1"),sQuery(id+"F0.wireOp",EDGE,"E7.1.2"),sQuery(id+"F0.wireOp",EDGE,"E7.1.3"),sQuery(id+"F0.wireOp",EDGE,"E7.2.0"),sQuery(id+"F0.wireOp",EDGE,"E7.2.1"),sQuery(id+"F0.wireOp",EDGE,"E7.2.2"),sQuery(id+"F0.wireOp",EDGE,"E7.2.3"),sQuery(id+"F0.wireOp",EDGE,"E8.trimOffspring"),sQuery(id+"F0.wireOp",EDGE,"E9.trimOffspring"),sQuery(id+"F0.wireOp",EDGE,"E10.4.3.0"),sQuery(id+"F0.wireOp",EDGE,"E10.8.3.0"),sQuery(id+"F0.wireOp",EDGE,"E10.11.3.0"),sQuery(id+"F0.wireOp",EDGE,"E10.12.3.0"),sQuery(id+"F0.wireOp",EDGE,"E11.trimOffspring")])],"isStart":true});
            var Q54;
            Q54=makeQuery(id+"FENhaPdsYRhXpVq_1.3.F5.boolean.opBoolean","MERGE",FACE,{"derivedFrom":[makeQuery(id+"F3.boolean.opBoolean","COPY",FACE,{"disambiguationData":[TD([makeQuery(id+"F1.opExtrude","SWEPT_FACE",FACE,{"disambiguationData":[OSD([sQuery(id+"F0.wireOp",EDGE,"E7.2.0")])]})])],"derivedFrom":makeQuery(id+"F3.opRevolve","SWEPT_FACE",FACE,{"disambiguationData":[OSD([sQuery(id+"F2.wireOp",EDGE,"E12.bottom")])]})}),makeQuery(id+"FENhaPdsYRhXpVq_1.3.F5.opExtrude","CAP_FACE",FACE,{"disambiguationData":[OSD([sQuery(id+"F4.wireOp",EDGE,"E15")])],"isStart":false})]});
            var Q55;
            {var subQ2=sQuery(id+"F0.wireOp",EDGE,"E4");Q55=makeQuery(id+"F3.boolean.opBoolean","SPLIT",FACE,{"disambiguationData":[TD([makeQuery(id+"F3.opRevolve","SWEPT_FACE",FACE,{"disambiguationData":[OSD([sQuery(id+"F2.wireOp",EDGE,"E12.top")])]})])],"derivedFrom":makeQuery(id+"F1.opExtrude","SWEPT_FACE",FACE,{"disambiguationData":[OSD([subQ2])]})});}
            var Q56;
            Q56=makeQuery(id+"F3.boolean.opBoolean","INTERSECT",EDGE,{"derivedFrom":[makeQuery(id+"F1.opExtrude","SWEPT_FACE",FACE,{"disambiguationData":[OSD([sQuery(id+"F0.wireOp",EDGE,"E10.8.3.0")])]}),makeQuery(id+"F3.opRevolve","SWEPT_FACE",FACE,{"disambiguationData":[OSD([sQuery(id+"F2.wireOp",EDGE,"E12.top")])]})]});
            var Q57;
            Q57=makeQuery(id+"F1.opExtrude","CAP_EDGE",EDGE,{"disambiguationData":[OSD([sQuery(id+"F0.wireOp",EDGE,"E4")])],"isStart":false});
            var Q58;
            {var subQ2=sQuery(id+"F0.wireOp",EDGE,"E10.4.3.0");Q58=makeQuery(id+"F3.boolean.opBoolean","SPLIT",FACE,{"disambiguationData":[TD([makeQuery(id+"F3.opRevolve","SWEPT_FACE",FACE,{"disambiguationData":[OSD([sQuery(id+"F2.wireOp",EDGE,"E12.top")])]})])],"derivedFrom":makeQuery(id+"F1.opExtrude","SWEPT_FACE",FACE,{"disambiguationData":[OSD([subQ2])]})});}
            var Q59;
            Q59=makeQuery(id+"F5.boolean.opBoolean","MERGE",FACE,{"derivedFrom":[makeQuery(id+"F3.boolean.opBoolean","COPY",FACE,{"disambiguationData":[TD([makeQuery(id+"F1.opExtrude","SWEPT_FACE",FACE,{"disambiguationData":[OSD([sQuery(id+"F0.wireOp",EDGE,"E10.4.3.0")])]})])],"derivedFrom":makeQuery(id+"F3.opRevolve","SWEPT_FACE",FACE,{"disambiguationData":[OSD([sQuery(id+"F2.wireOp",EDGE,"E12.top")])]})}),makeQuery(id+"F5.opExtrude","CAP_FACE",FACE,{"disambiguationData":[OSD([sQuery(id+"F4.wireOp",EDGE,"E15")])],"isStart":true})]});
            var Q60;
            Q60=makeQuery(id+"F3.boolean.opBoolean","INTERSECT",EDGE,{"derivedFrom":[makeQuery(id+"F1.opExtrude","SWEPT_FACE",FACE,{"disambiguationData":[OSD([sQuery(id+"F0.wireOp",EDGE,"E7.2.3")])]}),makeQuery(id+"F3.opRevolve","SWEPT_FACE",FACE,{"disambiguationData":[OSD([sQuery(id+"F2.wireOp",EDGE,"E12.top")])]})]});
            var Q61;
            Q61=makeQuery(id+"F1.opExtrude","CAP_EDGE",EDGE,{"disambiguationData":[OSD([sQuery(id+"F0.wireOp",EDGE,"E1")])],"isStart":false});
            var Q62;
            Q62=makeQuery(id+"F3.boolean.opBoolean","INTERSECT",EDGE,{"derivedFrom":[makeQuery(id+"F1.opExtrude","SWEPT_FACE",FACE,{"disambiguationData":[OSD([sQuery(id+"F0.wireOp",EDGE,"E5.filletArc")])]}),makeQuery(id+"F3.opRevolve","SWEPT_FACE",FACE,{"disambiguationData":[OSD([sQuery(id+"F2.wireOp",EDGE,"E12.top")])]})]});
            var Q63;
            {var subQ5=sQuery(id+"F0.wireOp",EDGE,"E6.filletArc");Q63=makeQuery(id+"F3.boolean.opBoolean","SPLIT",FACE,{"disambiguationData":[TD([makeQuery(id+"F3.opRevolve","SWEPT_FACE",FACE,{"disambiguationData":[OSD([sQuery(id+"F2.wireOp",EDGE,"E12.top")])]})])],"derivedFrom":makeQuery(id+"F1.opExtrude","SWEPT_FACE",FACE,{"disambiguationData":[OSD([subQ5])]})});}
            var Q64;
            {var subQ4=sQuery(id+"F0.wireOp",EDGE,"E7.2.0");Q64=makeQuery(id+"F3.boolean.opBoolean","SPLIT",FACE,{"disambiguationData":[TD([makeQuery(id+"F3.opRevolve","SWEPT_FACE",FACE,{"disambiguationData":[OSD([sQuery(id+"F2.wireOp",EDGE,"E12.bottom")])]})])],"derivedFrom":makeQuery(id+"F1.opExtrude","SWEPT_FACE",FACE,{"disambiguationData":[OSD([subQ4])]})});}
            var Q65;
            {var subQ2=sQuery(id+"F0.wireOp",EDGE,"E10.4.3.0");Q65=makeQuery(id+"F3.boolean.opBoolean","SPLIT",FACE,{"disambiguationData":[TD([makeQuery(id+"F3.opRevolve","SWEPT_FACE",FACE,{"disambiguationData":[OSD([sQuery(id+"F2.wireOp",EDGE,"E12.bottom")])]})])],"derivedFrom":makeQuery(id+"F1.opExtrude","SWEPT_FACE",FACE,{"disambiguationData":[OSD([subQ2])]})});}
            var Q66;
            Q66=makeQuery(id+"F1.opExtrude","CAP_EDGE",EDGE,{"disambiguationData":[OSD([sQuery(id+"F0.wireOp",EDGE,"E10.8.3.0")])],"isStart":false});
            var Q67;
            Q67=makeQuery(id+"FENhaPdsYRhXpVq_1.1.F5.boolean.opBoolean","COPY",FACE,{"derivedFrom":makeQuery(id+"FENhaPdsYRhXpVq_1.1.F5.opExtrude","SWEPT_FACE",FACE,{"disambiguationData":[OSD([sQuery(id+"F4.wireOp",EDGE,"E15")])]})});
            var Q68;
            Q68=makeQuery(id+"F1.opExtrude","CAP_EDGE",EDGE,{"disambiguationData":[OSD([sQuery(id+"F0.wireOp",EDGE,"E7.2.3")])],"isStart":false});
            var Q69;
            Q69=makeQuery(id+"F1.opExtrude","CAP_EDGE",EDGE,{"disambiguationData":[OSD([sQuery(id+"F0.wireOp",EDGE,"E11.trimOffspring")])],"isStart":true});
            var Q70;
            Q70=makeQuery(id+"F1.opExtrude","CAP_EDGE",EDGE,{"disambiguationData":[OSD([sQuery(id+"F0.wireOp",EDGE,"E9.trimOffspring")])],"isStart":false});
            var Q71;
            {var subQ5=sQuery(id+"F0.wireOp",EDGE,"E7.1.0");Q71=makeQuery(id+"F3.boolean.opBoolean","SPLIT",FACE,{"disambiguationData":[TD([makeQuery(id+"F3.opRevolve","SWEPT_FACE",FACE,{"disambiguationData":[OSD([sQuery(id+"F2.wireOp",EDGE,"E12.bottom")])]})])],"derivedFrom":makeQuery(id+"F1.opExtrude","SWEPT_FACE",FACE,{"disambiguationData":[OSD([subQ5])]})});}
            var Q72;
            Q72=makeQuery(id+"F1.opExtrude","SWEPT_FACE",FACE,{"disambiguationData":[OSD([sQuery(id+"F0.wireOp",EDGE,"E0")])]});
            var Q73;
            {var subQ0=sQuery(id+"F0.wireOp",EDGE,"E7.2.3");Q73=makeQuery(id+"F3.boolean.opBoolean","SPLIT",FACE,{"disambiguationData":[TD([makeQuery(id+"F3.opRevolve","SWEPT_FACE",FACE,{"disambiguationData":[OSD([sQuery(id+"F2.wireOp",EDGE,"E12.bottom")])]})])],"derivedFrom":makeQuery(id+"F1.opExtrude","SWEPT_FACE",FACE,{"disambiguationData":[OSD([subQ0])]})});}
            var Q74;
            Q74=makeQuery(id+"F3.boolean.opBoolean","INTERSECT",EDGE,{"derivedFrom":[makeQuery(id+"F1.opExtrude","SWEPT_FACE",FACE,{"disambiguationData":[OSD([sQuery(id+"F0.wireOp",EDGE,"E6.filletArc")])]}),makeQuery(id+"F3.opRevolve","SWEPT_FACE",FACE,{"disambiguationData":[OSD([sQuery(id+"F2.wireOp",EDGE,"E12.top")])]})]});
            var Q75;
            Q75=makeQuery(id+"F3.boolean.opBoolean","INTERSECT",EDGE,{"derivedFrom":[makeQuery(id+"F1.opExtrude","SWEPT_FACE",FACE,{"disambiguationData":[OSD([sQuery(id+"F0.wireOp",EDGE,"E6.filletArc")])]}),makeQuery(id+"F3.opRevolve","SWEPT_FACE",FACE,{"disambiguationData":[OSD([sQuery(id+"F2.wireOp",EDGE,"E12.bottom")])]})]});
            var Q76;
            Q76=makeQuery(id+"F1.opExtrude","CAP_EDGE",EDGE,{"disambiguationData":[OSD([sQuery(id+"F0.wireOp",EDGE,"E7.1.2")])],"isStart":false});
            var Q77;
            {var subQ4=sQuery(id+"F0.wireOp",EDGE,"E10.8.3.0");Q77=makeQuery(id+"F3.boolean.opBoolean","SPLIT",FACE,{"disambiguationData":[TD([makeQuery(id+"F3.opRevolve","SWEPT_FACE",FACE,{"disambiguationData":[OSD([sQuery(id+"F2.wireOp",EDGE,"E12.bottom")])]})])],"derivedFrom":makeQuery(id+"F1.opExtrude","SWEPT_FACE",FACE,{"disambiguationData":[OSD([subQ4])]})});}
            var Q78;
            {var subQ0=sQuery(id+"F0.wireOp",EDGE,"E10.12.3.0");Q78=makeQuery(id+"F3.boolean.opBoolean","SPLIT",FACE,{"disambiguationData":[TD([makeQuery(id+"F3.opRevolve","SWEPT_FACE",FACE,{"disambiguationData":[OSD([sQuery(id+"F2.wireOp",EDGE,"E12.bottom")])]})])],"derivedFrom":makeQuery(id+"F1.opExtrude","SWEPT_FACE",FACE,{"disambiguationData":[OSD([subQ0])]})});}
            var Q79;
            {var subQ5=sQuery(id+"F0.wireOp",EDGE,"E6.filletArc");Q79=makeQuery(id+"F3.boolean.opBoolean","SPLIT",FACE,{"disambiguationData":[TD([makeQuery(id+"F3.opRevolve","SWEPT_FACE",FACE,{"disambiguationData":[OSD([sQuery(id+"F2.wireOp",EDGE,"E12.bottom")])]})])],"derivedFrom":makeQuery(id+"F1.opExtrude","SWEPT_FACE",FACE,{"disambiguationData":[OSD([subQ5])]})});}
            var Q80;
            {var subQ5=sQuery(id+"F0.wireOp",EDGE,"E5.filletArc");Q80=makeQuery(id+"F3.boolean.opBoolean","SPLIT",FACE,{"disambiguationData":[TD([makeQuery(id+"F3.opRevolve","SWEPT_FACE",FACE,{"disambiguationData":[OSD([sQuery(id+"F2.wireOp",EDGE,"E12.bottom")])]})])],"derivedFrom":makeQuery(id+"F1.opExtrude","SWEPT_FACE",FACE,{"disambiguationData":[OSD([subQ5])]})});}
            var Q81;
            Q81=makeQuery(id+"FENhaPdsYRhXpVq_1.1.F5.boolean.opBoolean","MERGE",FACE,{"derivedFrom":[makeQuery(id+"F3.boolean.opBoolean","COPY",FACE,{"disambiguationData":[TD([makeQuery(id+"F1.opExtrude","SWEPT_FACE",FACE,{"disambiguationData":[OSD([sQuery(id+"F0.wireOp",EDGE,"E2")])]})])],"derivedFrom":makeQuery(id+"F3.opRevolve","SWEPT_FACE",FACE,{"disambiguationData":[OSD([sQuery(id+"F2.wireOp",EDGE,"E12.bottom")])]})}),makeQuery(id+"FENhaPdsYRhXpVq_1.1.F5.opExtrude","CAP_FACE",FACE,{"disambiguationData":[OSD([sQuery(id+"F4.wireOp",EDGE,"E15")])],"isStart":false})]});
            var Q82;
            Q82=makeQuery(id+"F3.boolean.opBoolean","INTERSECT",EDGE,{"derivedFrom":[makeQuery(id+"F1.opExtrude","SWEPT_FACE",FACE,{"disambiguationData":[OSD([sQuery(id+"F0.wireOp",EDGE,"E10.11.3.0")])]}),makeQuery(id+"F3.opRevolve","SWEPT_FACE",FACE,{"disambiguationData":[OSD([sQuery(id+"F2.wireOp",EDGE,"E12.top")])]})]});
            var Q83;
            {var subQ2=sQuery(id+"F0.wireOp",EDGE,"E1");var subQ3=makeQuery(id+"F1.opExtrude","SWEPT_FACE",FACE,{"disambiguationData":[OSD([subQ2])]});var subQ4=makeQuery(id+"F3.opRevolve","SWEPT_FACE",FACE,{"disambiguationData":[OSD([sQuery(id+"F2.wireOp",EDGE,"E12.right")])]});var subQ5=sQuery(id+"F0.wireOp",EDGE,"E7.2.0");var subQ6=makeQuery(id+"F1.opExtrude","SWEPT_FACE",FACE,{"disambiguationData":[OSD([subQ5])]});var subQ11=sQuery(id+"F0.wireOp",EDGE,"E8.trimOffspring");var subQ12=makeQuery(id+"F1.opExtrude","SWEPT_FACE",FACE,{"disambiguationData":[OSD([subQ11])]});var subQ13=sQuery(id+"F0.wireOp",EDGE,"E9.trimOffspring");var subQ14=makeQuery(id+"F1.opExtrude","SWEPT_FACE",FACE,{"disambiguationData":[OSD([subQ13])]});var subQ15=sQuery(id+"F0.wireOp",EDGE,"E11.trimOffspring");var subQ16=makeQuery(id+"F1.opExtrude","SWEPT_FACE",FACE,{"disambiguationData":[OSD([subQ15])]});var subQ30=sQuery(id+"F0.wireOp",EDGE,"E7.1.0");var subQ32=sQuery(id+"F0.wireOp",EDGE,"E5.filletArc");var subQ48=makeQuery(id+"F1.opExtrude","SWEPT_FACE",FACE,{"disambiguationData":[OSD([subQ30])]});var subQ52=makeQuery(id+"F1.opExtrude","SWEPT_FACE",FACE,{"disambiguationData":[OSD([subQ32])]});Q83=makeQuery(id+"FENhaPdsYRhXpVq_1.3.F5.boolean.opBoolean","SPLIT",FACE,{"disambiguationData":[TD([subQ6])],"derivedFrom":makeQuery(id+"FENhaPdsYRhXpVq_1.2.F5.boolean.opBoolean","SPLIT",FACE,{"disambiguationData":[TD([subQ48])],"derivedFrom":makeQuery(id+"FENhaPdsYRhXpVq_1.1.F5.boolean.opBoolean","SPLIT",FACE,{"disambiguationData":[TD([subQ52])],"derivedFrom":makeQuery(id+"F3.boolean.opBoolean","MERGE",FACE,{"derivedFrom":[subQ3,subQ12,subQ14,subQ16,subQ4]})})})});}
            var Q84;
            Q84=makeQuery(id+"F3.boolean.opBoolean","INTERSECT",EDGE,{"derivedFrom":[makeQuery(id+"F1.opExtrude","SWEPT_FACE",FACE,{"disambiguationData":[OSD([sQuery(id+"F0.wireOp",EDGE,"E7.2.0")])]}),makeQuery(id+"F3.opRevolve","SWEPT_FACE",FACE,{"disambiguationData":[OSD([sQuery(id+"F2.wireOp",EDGE,"E12.bottom")])]})]});
            var Q85;
            {var subQ0=sQuery(id+"F0.wireOp",EDGE,"E7.1.3");Q85=makeQuery(id+"F3.boolean.opBoolean","SPLIT",FACE,{"disambiguationData":[TD([makeQuery(id+"F3.opRevolve","SWEPT_FACE",FACE,{"disambiguationData":[OSD([sQuery(id+"F2.wireOp",EDGE,"E12.bottom")])]})])],"derivedFrom":makeQuery(id+"F1.opExtrude","SWEPT_FACE",FACE,{"disambiguationData":[OSD([subQ0])]})});}
            var Q86;
            {var subQ2=sQuery(id+"F0.wireOp",EDGE,"E5.filletArc");var subQ3=makeQuery(id+"F1.opExtrude","SWEPT_FACE",FACE,{"disambiguationData":[OSD([subQ2])]});var subQ4=sQuery(id+"F0.wireOp",EDGE,"E9.trimOffspring");var subQ5=makeQuery(id+"F1.opExtrude","SWEPT_FACE",FACE,{"disambiguationData":[OSD([subQ4])]});var subQ8=sQuery(id+"F0.wireOp",EDGE,"E8.trimOffspring");var subQ9=makeQuery(id+"F1.opExtrude","SWEPT_FACE",FACE,{"disambiguationData":[OSD([subQ8])]});var subQ12=sQuery(id+"F0.wireOp",EDGE,"E1");var subQ13=makeQuery(id+"F1.opExtrude","SWEPT_FACE",FACE,{"disambiguationData":[OSD([subQ12])]});var subQ14=makeQuery(id+"F3.opRevolve","SWEPT_FACE",FACE,{"disambiguationData":[OSD([sQuery(id+"F2.wireOp",EDGE,"E12.right")])]});var subQ17=sQuery(id+"F0.wireOp",EDGE,"E11.trimOffspring");var subQ18=makeQuery(id+"F1.opExtrude","SWEPT_FACE",FACE,{"disambiguationData":[OSD([subQ17])]});Q86=makeQuery(id+"FENhaPdsYRhXpVq_1.2.F5.boolean.opBoolean","SPLIT",FACE,{"disambiguationData":[TD([subQ3])],"derivedFrom":makeQuery(id+"FENhaPdsYRhXpVq_1.1.F5.boolean.opBoolean","SPLIT",FACE,{"disambiguationData":[TD([subQ3])],"derivedFrom":makeQuery(id+"F3.boolean.opBoolean","MERGE",FACE,{"derivedFrom":[subQ13,subQ9,subQ5,subQ18,subQ14]})})});}
            var Q87;
            {var subQ5=sQuery(id+"F0.wireOp",EDGE,"E5.filletArc");Q87=makeQuery(id+"F3.boolean.opBoolean","SPLIT",FACE,{"disambiguationData":[TD([makeQuery(id+"F3.opRevolve","SWEPT_FACE",FACE,{"disambiguationData":[OSD([sQuery(id+"F2.wireOp",EDGE,"E12.top")])]})])],"derivedFrom":makeQuery(id+"F1.opExtrude","SWEPT_FACE",FACE,{"disambiguationData":[OSD([subQ5])]})});}
            var Q88;
            Q88=makeQuery(id+"F3.boolean.opBoolean","INTERSECT",EDGE,{"derivedFrom":[makeQuery(id+"F1.opExtrude","SWEPT_FACE",FACE,{"disambiguationData":[OSD([sQuery(id+"F0.wireOp",EDGE,"E10.12.3.0")])]}),makeQuery(id+"F3.opRevolve","SWEPT_FACE",FACE,{"disambiguationData":[OSD([sQuery(id+"F2.wireOp",EDGE,"E12.top")])]})]});
            var Q89;
            Q89=makeQuery(id+"F5.boolean.opBoolean","MERGE",FACE,{"derivedFrom":[makeQuery(id+"F3.boolean.opBoolean","COPY",FACE,{"disambiguationData":[TD([makeQuery(id+"F1.opExtrude","SWEPT_FACE",FACE,{"disambiguationData":[OSD([sQuery(id+"F0.wireOp",EDGE,"E10.4.3.0")])]})])],"derivedFrom":makeQuery(id+"F3.opRevolve","SWEPT_FACE",FACE,{"disambiguationData":[OSD([sQuery(id+"F2.wireOp",EDGE,"E12.bottom")])]})}),makeQuery(id+"F5.opExtrude","CAP_FACE",FACE,{"disambiguationData":[OSD([sQuery(id+"F4.wireOp",EDGE,"E15")])],"isStart":false})]});
            var Q90;
            {var subQ2=sQuery(id+"F0.wireOp",EDGE,"E4");Q90=makeQuery(id+"F3.boolean.opBoolean","SPLIT",FACE,{"disambiguationData":[TD([makeQuery(id+"F3.opRevolve","SWEPT_FACE",FACE,{"disambiguationData":[OSD([sQuery(id+"F2.wireOp",EDGE,"E12.bottom")])]})])],"derivedFrom":makeQuery(id+"F1.opExtrude","SWEPT_FACE",FACE,{"disambiguationData":[OSD([subQ2])]})});}
            var Q91;
            Q91=makeQuery(id+"F3.boolean.opBoolean","INTERSECT",EDGE,{"derivedFrom":[makeQuery(id+"F1.opExtrude","SWEPT_FACE",FACE,{"disambiguationData":[OSD([sQuery(id+"F0.wireOp",EDGE,"E4")])]}),makeQuery(id+"F3.opRevolve","SWEPT_FACE",FACE,{"disambiguationData":[OSD([sQuery(id+"F2.wireOp",EDGE,"E12.top")])]})]});
            var Q92;
            {var subQ0=sQuery(id+"F0.wireOp",EDGE,"E1");var subQ2=sQuery(id+"F0.wireOp",EDGE,"E5.filletArc");Q92=makeQuery(id+"F3.boolean.opBoolean","SPLIT",EDGE,{"disambiguationData":[TD([makeQuery(id+"F3.opRevolve","SWEPT_FACE",FACE,{"disambiguationData":[OSD([sQuery(id+"F2.wireOp",EDGE,"E12.top")])]})])],"derivedFrom":makeQuery(id+"F1.opExtrude","SWEPT_EDGE",EDGE,{"disambiguationData":[OSD([subQ0,subQ2])]})});}
            var Q93;
            Q93=makeQuery(id+"F3.boolean.opBoolean","INTERSECT",EDGE,{"derivedFrom":[makeQuery(id+"F1.opExtrude","SWEPT_FACE",FACE,{"disambiguationData":[OSD([sQuery(id+"F0.wireOp",EDGE,"E10.12.3.0")])]}),makeQuery(id+"F3.opRevolve","SWEPT_FACE",FACE,{"disambiguationData":[OSD([sQuery(id+"F2.wireOp",EDGE,"E12.bottom")])]})]});
            var Q94;
            {var subQ2=sQuery(id+"F0.wireOp",EDGE,"E6.filletArc");var subQ4=sQuery(id+"F0.wireOp",EDGE,"E9.trimOffspring");Q94=makeQuery(id+"F3.boolean.opBoolean","SPLIT",EDGE,{"disambiguationData":[TD([makeQuery(id+"F3.opRevolve","SWEPT_FACE",FACE,{"disambiguationData":[OSD([sQuery(id+"F2.wireOp",EDGE,"E12.bottom")])]})])],"derivedFrom":makeQuery(id+"F1.opExtrude","SWEPT_EDGE",EDGE,{"disambiguationData":[OSD([subQ2,subQ4])]})});}
            var Q95;
            {var subQ5=sQuery(id+"F0.wireOp",EDGE,"E7.1.0");Q95=makeQuery(id+"F3.boolean.opBoolean","SPLIT",FACE,{"disambiguationData":[TD([makeQuery(id+"F3.opRevolve","SWEPT_FACE",FACE,{"disambiguationData":[OSD([sQuery(id+"F2.wireOp",EDGE,"E12.top")])]})])],"derivedFrom":makeQuery(id+"F1.opExtrude","SWEPT_FACE",FACE,{"disambiguationData":[OSD([subQ5])]})});}
            var Q96;
            {var subQ0=sQuery(id+"F0.wireOp",EDGE,"E10.8.3.0");var subQ1=sQuery(id+"F0.wireOp",EDGE,"E10.4.3.0");Q96=makeQuery(id+"F3.boolean.opBoolean","SPLIT",EDGE,{"disambiguationData":[TD([makeQuery(id+"F3.opRevolve","SWEPT_FACE",FACE,{"disambiguationData":[OSD([sQuery(id+"F2.wireOp",EDGE,"E12.top")])]})])],"derivedFrom":makeQuery(id+"F1.opExtrude","SWEPT_EDGE",EDGE,{"disambiguationData":[OSD([subQ1,subQ0])]})});}
            var Q97;
            Q97=makeQuery(id+"F1.opExtrude","CAP_EDGE",EDGE,{"disambiguationData":[OSD([sQuery(id+"F0.wireOp",EDGE,"E7.1.3")])],"isStart":true});
            var Q98;
            Q98=makeQuery(id+"FENhaPdsYRhXpVq_1.3.F5.boolean.opBoolean","COPY",FACE,{"derivedFrom":makeQuery(id+"FENhaPdsYRhXpVq_1.3.F5.opExtrude","SWEPT_FACE",FACE,{"disambiguationData":[OSD([sQuery(id+"F4.wireOp",EDGE,"E15")])]})});
            var Q99;
            {var subQ2=makeQuery(id+"F1.opExtrude","SWEPT_FACE",FACE,{"disambiguationData":[OSD([sQuery(id+"F0.wireOp",EDGE,"E7.2.0")])]});var subQ4=sQuery(id+"F2.wireOp",EDGE,"E12.right");var subQ8=sQuery(id+"F2.wireOp",EDGE,"E12.bottom");Q99=makeQuery(id+"FENhaPdsYRhXpVq_1.3.F5.boolean.opBoolean","SPLIT",EDGE,{"disambiguationData":[TD([subQ2])],"derivedFrom":makeQuery(id+"F3.boolean.opBoolean","COPY",EDGE,{"disambiguationData":[TD([subQ2])],"derivedFrom":makeQuery(id+"F3.opRevolve","SWEPT_EDGE",EDGE,{"disambiguationData":[OSD([subQ8,subQ4])]})})});}
            var Q100;
            {var subQ3=sQuery(id+"F0.wireOp",EDGE,"E11.trimOffspring");var subQ4=sQuery(id+"F0.wireOp",EDGE,"E10.8.3.0");Q100=makeQuery(id+"F3.boolean.opBoolean","SPLIT",EDGE,{"disambiguationData":[TD([makeQuery(id+"F3.opRevolve","SWEPT_FACE",FACE,{"disambiguationData":[OSD([sQuery(id+"F2.wireOp",EDGE,"E12.bottom")])]})])],"derivedFrom":makeQuery(id+"F1.opExtrude","SWEPT_EDGE",EDGE,{"disambiguationData":[OSD([subQ4,subQ3])]})});}
            var Q101;
            {var subQ0=sQuery(id+"F0.wireOp",EDGE,"E8.trimOffspring");var subQ1=sQuery(id+"F0.wireOp",EDGE,"E7.2.2");Q101=makeQuery(id+"F3.boolean.opBoolean","SPLIT",EDGE,{"disambiguationData":[TD([makeQuery(id+"F3.opRevolve","SWEPT_FACE",FACE,{"disambiguationData":[OSD([sQuery(id+"F2.wireOp",EDGE,"E12.bottom")])]})])],"derivedFrom":makeQuery(id+"F1.opExtrude","SWEPT_EDGE",EDGE,{"disambiguationData":[OSD([subQ1,subQ0])]})});}
            var Q102;
            {var subQ0=sQuery(id+"F0.wireOp",EDGE,"E5.filletArc");var subQ1=sQuery(id+"F0.wireOp",EDGE,"E4");Q102=makeQuery(id+"F3.boolean.opBoolean","SPLIT",EDGE,{"disambiguationData":[TD([makeQuery(id+"F3.opRevolve","SWEPT_FACE",FACE,{"disambiguationData":[OSD([sQuery(id+"F2.wireOp",EDGE,"E12.top")])]})])],"derivedFrom":makeQuery(id+"F1.opExtrude","SWEPT_EDGE",EDGE,{"disambiguationData":[OSD([subQ1,subQ0])]})});}
            var Q103;
            Q103=makeQuery(id+"F3.boolean.opBoolean","INTERSECT",EDGE,{"derivedFrom":[makeQuery(id+"F1.opExtrude","SWEPT_FACE",FACE,{"disambiguationData":[OSD([sQuery(id+"F0.wireOp",EDGE,"E5.filletArc")])]}),makeQuery(id+"F3.opRevolve","SWEPT_FACE",FACE,{"disambiguationData":[OSD([sQuery(id+"F2.wireOp",EDGE,"E12.bottom")])]})]});
            var Q104;
            {var subQ2=makeQuery(id+"F1.opExtrude","SWEPT_FACE",FACE,{"disambiguationData":[OSD([sQuery(id+"F0.wireOp",EDGE,"E7.2.0")])]});var subQ4=sQuery(id+"F2.wireOp",EDGE,"E12.right");var subQ8=sQuery(id+"F2.wireOp",EDGE,"E12.top");Q104=makeQuery(id+"FENhaPdsYRhXpVq_1.3.F5.boolean.opBoolean","SPLIT",EDGE,{"disambiguationData":[TD([subQ2])],"derivedFrom":makeQuery(id+"F3.boolean.opBoolean","COPY",EDGE,{"disambiguationData":[TD([subQ2])],"derivedFrom":makeQuery(id+"F3.opRevolve","SWEPT_EDGE",EDGE,{"disambiguationData":[OSD([subQ8,subQ4])]})})});}
            var Q105;
            {var subQ1=makeQuery(id+"F1.opExtrude","SWEPT_FACE",FACE,{"disambiguationData":[OSD([sQuery(id+"F0.wireOp",EDGE,"E5.filletArc")])]});var subQ4=sQuery(id+"F2.wireOp",EDGE,"E12.right");var subQ6=makeQuery(id+"F1.opExtrude","SWEPT_FACE",FACE,{"disambiguationData":[OSD([sQuery(id+"F0.wireOp",EDGE,"E6.filletArc")])]});var subQ8=sQuery(id+"F2.wireOp",EDGE,"E12.bottom");Q105=makeQuery(id+"FENhaPdsYRhXpVq_1.1.F5.boolean.opBoolean","SPLIT",EDGE,{"disambiguationData":[TD([subQ6])],"derivedFrom":makeQuery(id+"F3.boolean.opBoolean","COPY",EDGE,{"disambiguationData":[TD([subQ1])],"derivedFrom":makeQuery(id+"F3.opRevolve","SWEPT_EDGE",EDGE,{"disambiguationData":[OSD([subQ8,subQ4])]})})});}
            var Q106;
            {var subQ0=sQuery(id+"F0.wireOp",EDGE,"E10.11.3.0");var subQ1=sQuery(id+"F0.wireOp",EDGE,"E10.4.3.0");Q106=makeQuery(id+"F3.boolean.opBoolean","SPLIT",EDGE,{"disambiguationData":[TD([makeQuery(id+"F3.opRevolve","SWEPT_FACE",FACE,{"disambiguationData":[OSD([sQuery(id+"F2.wireOp",EDGE,"E12.top")])]})])],"derivedFrom":makeQuery(id+"F1.opExtrude","SWEPT_EDGE",EDGE,{"disambiguationData":[OSD([subQ1,subQ0])]})});}
            var Q107;
            Q107=makeQuery(id+"F1.opExtrude","CAP_EDGE",EDGE,{"disambiguationData":[OSD([sQuery(id+"F0.wireOp",EDGE,"E7.1.0")])],"isStart":true});
            var Q108;
            Q108=makeQuery(id+"F5.boolean.opBoolean","COPY",EDGE,{"derivedFrom":makeQuery(id+"F5.opExtrude","CAP_EDGE",EDGE,{"disambiguationData":[OSD([sQuery(id+"F4.wireOp",EDGE,"E15")])],"isStart":false})});
            var Q109;
            Q109=makeQuery(id+"F1.opExtrude","CAP_EDGE",EDGE,{"disambiguationData":[OSD([sQuery(id+"F0.wireOp",EDGE,"E1")])],"isStart":true});
            var Q110;
            {var subQ2=sQuery(id+"F0.wireOp",EDGE,"E7.2.0");var subQ3=sQuery(id+"F0.wireOp",EDGE,"E11.trimOffspring");Q110=makeQuery(id+"F3.boolean.opBoolean","SPLIT",EDGE,{"disambiguationData":[TD([makeQuery(id+"F3.opRevolve","SWEPT_FACE",FACE,{"disambiguationData":[OSD([sQuery(id+"F2.wireOp",EDGE,"E12.bottom")])]})])],"derivedFrom":makeQuery(id+"F1.opExtrude","SWEPT_EDGE",EDGE,{"disambiguationData":[OSD([subQ2,subQ3])]})});}
            var Q111;
            Q111=makeQuery(id+"F3.boolean.opBoolean","INTERSECT",EDGE,{"derivedFrom":[makeQuery(id+"F1.opExtrude","SWEPT_FACE",FACE,{"disambiguationData":[OSD([sQuery(id+"F0.wireOp",EDGE,"E7.1.1")])]}),makeQuery(id+"F3.opRevolve","SWEPT_FACE",FACE,{"disambiguationData":[OSD([sQuery(id+"F2.wireOp",EDGE,"E12.top")])]})]});
            var Q112;
            {var subQ0=sQuery(id+"F0.wireOp",EDGE,"E6.filletArc");var subQ4=sQuery(id+"F0.wireOp",EDGE,"E9.trimOffspring");Q112=makeQuery(id+"F3.boolean.opBoolean","SPLIT",EDGE,{"disambiguationData":[TD([makeQuery(id+"F3.opRevolve","SWEPT_FACE",FACE,{"disambiguationData":[OSD([sQuery(id+"F2.wireOp",EDGE,"E12.top")])]})])],"derivedFrom":makeQuery(id+"F1.opExtrude","SWEPT_EDGE",EDGE,{"disambiguationData":[OSD([subQ0,subQ4])]})});}
            var Q113;
            Q113=makeQuery(id+"F5.boolean.opBoolean","COPY",EDGE,{"derivedFrom":makeQuery(id+"F5.opExtrude","CAP_EDGE",EDGE,{"disambiguationData":[OSD([sQuery(id+"F4.wireOp",EDGE,"E15")])],"isStart":true})});
            var Q114;
            {var subQ0=sQuery(id+"F0.wireOp",EDGE,"E7.1.1");var subQ1=sQuery(id+"F0.wireOp",EDGE,"E7.1.0");Q114=makeQuery(id+"F3.boolean.opBoolean","SPLIT",EDGE,{"disambiguationData":[TD([makeQuery(id+"F3.opRevolve","SWEPT_FACE",FACE,{"disambiguationData":[OSD([sQuery(id+"F2.wireOp",EDGE,"E12.bottom")])]})])],"derivedFrom":makeQuery(id+"F1.opExtrude","SWEPT_EDGE",EDGE,{"disambiguationData":[OSD([subQ1,subQ0])]})});}
            var Q115;
            Q115=makeQuery(id+"F3.boolean.opBoolean","INTERSECT",EDGE,{"derivedFrom":[makeQuery(id+"F1.opExtrude","SWEPT_FACE",FACE,{"disambiguationData":[OSD([sQuery(id+"F0.wireOp",EDGE,"E2")])]}),makeQuery(id+"F3.opRevolve","SWEPT_FACE",FACE,{"disambiguationData":[OSD([sQuery(id+"F2.wireOp",EDGE,"E12.bottom")])]})]});
            var Q116;
            {var subQ0=makeQuery(id+"F1.opExtrude","SWEPT_FACE",FACE,{"disambiguationData":[OSD([sQuery(id+"F0.wireOp",EDGE,"E10.11.3.0")])]});var subQ5=sQuery(id+"F2.wireOp",EDGE,"E12.right");var subQ8=makeQuery(id+"F1.opExtrude","SWEPT_FACE",FACE,{"disambiguationData":[OSD([sQuery(id+"F0.wireOp",EDGE,"E10.8.3.0")])]});var subQ9=sQuery(id+"F2.wireOp",EDGE,"E12.bottom");Q116=makeQuery(id+"F5.boolean.opBoolean","SPLIT",EDGE,{"disambiguationData":[TD([subQ0])],"derivedFrom":makeQuery(id+"F3.boolean.opBoolean","COPY",EDGE,{"disambiguationData":[TD([subQ8])],"derivedFrom":makeQuery(id+"F3.opRevolve","SWEPT_EDGE",EDGE,{"disambiguationData":[OSD([subQ9,subQ5])]})})});}
            var Q117;
            Q117=makeQuery(id+"F5.boolean.opBoolean","INTERSECT",EDGE,{"disambiguationData":[OD(0.0)],"derivedFrom":[makeQuery(id+"F3.boolean.opBoolean","MERGE",FACE,{"derivedFrom":[makeQuery(id+"F1.opExtrude","SWEPT_FACE",FACE,{"disambiguationData":[OSD([sQuery(id+"F0.wireOp",EDGE,"E1")])]}),makeQuery(id+"F1.opExtrude","SWEPT_FACE",FACE,{"disambiguationData":[OSD([sQuery(id+"F0.wireOp",EDGE,"E8.trimOffspring")])]}),makeQuery(id+"F1.opExtrude","SWEPT_FACE",FACE,{"disambiguationData":[OSD([sQuery(id+"F0.wireOp",EDGE,"E9.trimOffspring")])]}),makeQuery(id+"F1.opExtrude","SWEPT_FACE",FACE,{"disambiguationData":[OSD([sQuery(id+"F0.wireOp",EDGE,"E11.trimOffspring")])]}),makeQuery(id+"F3.opRevolve","SWEPT_FACE",FACE,{"disambiguationData":[OSD([sQuery(id+"F2.wireOp",EDGE,"E12.right")])]})]}),makeQuery(id+"F5.opExtrude","SWEPT_FACE",FACE,{"disambiguationData":[OSD([sQuery(id+"F4.wireOp",EDGE,"E15")])]})]});
            var Q118;
            Q118=makeQuery(id+"F1.opExtrude","CAP_EDGE",EDGE,{"disambiguationData":[OSD([sQuery(id+"F0.wireOp",EDGE,"E10.12.3.0")])],"isStart":true});
            var Q119;
            {var subQ2=makeQuery(id+"F1.opExtrude","SWEPT_FACE",FACE,{"disambiguationData":[OSD([sQuery(id+"F0.wireOp",EDGE,"E7.2.2")])]});var subQ4=sQuery(id+"F2.wireOp",EDGE,"E12.right");var subQ7=makeQuery(id+"F1.opExtrude","SWEPT_FACE",FACE,{"disambiguationData":[OSD([sQuery(id+"F0.wireOp",EDGE,"E7.2.0")])]});var subQ8=sQuery(id+"F2.wireOp",EDGE,"E12.bottom");Q119=makeQuery(id+"FENhaPdsYRhXpVq_1.3.F5.boolean.opBoolean","SPLIT",EDGE,{"disambiguationData":[TD([subQ2])],"derivedFrom":makeQuery(id+"F3.boolean.opBoolean","COPY",EDGE,{"disambiguationData":[TD([subQ7])],"derivedFrom":makeQuery(id+"F3.opRevolve","SWEPT_EDGE",EDGE,{"disambiguationData":[OSD([subQ8,subQ4])]})})});}
            var Q120;
            Q120=makeQuery(id+"FENhaPdsYRhXpVq_1.1.F5.boolean.opBoolean","INTERSECT",EDGE,{"disambiguationData":[OD(0.0)],"derivedFrom":[makeQuery(id+"F3.boolean.opBoolean","MERGE",FACE,{"derivedFrom":[makeQuery(id+"F1.opExtrude","SWEPT_FACE",FACE,{"disambiguationData":[OSD([sQuery(id+"F0.wireOp",EDGE,"E1")])]}),makeQuery(id+"F1.opExtrude","SWEPT_FACE",FACE,{"disambiguationData":[OSD([sQuery(id+"F0.wireOp",EDGE,"E8.trimOffspring")])]}),makeQuery(id+"F1.opExtrude","SWEPT_FACE",FACE,{"disambiguationData":[OSD([sQuery(id+"F0.wireOp",EDGE,"E9.trimOffspring")])]}),makeQuery(id+"F1.opExtrude","SWEPT_FACE",FACE,{"disambiguationData":[OSD([sQuery(id+"F0.wireOp",EDGE,"E11.trimOffspring")])]}),makeQuery(id+"F3.opRevolve","SWEPT_FACE",FACE,{"disambiguationData":[OSD([sQuery(id+"F2.wireOp",EDGE,"E12.right")])]})]}),makeQuery(id+"FENhaPdsYRhXpVq_1.1.F5.opExtrude","SWEPT_FACE",FACE,{"disambiguationData":[OSD([sQuery(id+"F4.wireOp",EDGE,"E15")])]})]});
            var Q121;
            {var subQ3=sQuery(id+"F0.wireOp",EDGE,"E11.trimOffspring");var subQ4=sQuery(id+"F0.wireOp",EDGE,"E10.8.3.0");Q121=makeQuery(id+"F3.boolean.opBoolean","SPLIT",EDGE,{"disambiguationData":[TD([makeQuery(id+"F3.opRevolve","SWEPT_FACE",FACE,{"disambiguationData":[OSD([sQuery(id+"F2.wireOp",EDGE,"E12.top")])]})])],"derivedFrom":makeQuery(id+"F1.opExtrude","SWEPT_EDGE",EDGE,{"disambiguationData":[OSD([subQ4,subQ3])]})});}
            var Q122;
            {var subQ1=makeQuery(id+"F1.opExtrude","SWEPT_FACE",FACE,{"disambiguationData":[OSD([sQuery(id+"F0.wireOp",EDGE,"E5.filletArc")])]});var subQ4=sQuery(id+"F2.wireOp",EDGE,"E12.right");var subQ9=sQuery(id+"F2.wireOp",EDGE,"E12.top");Q122=makeQuery(id+"FENhaPdsYRhXpVq_1.1.F5.boolean.opBoolean","SPLIT",EDGE,{"disambiguationData":[TD([subQ1])],"derivedFrom":makeQuery(id+"F3.boolean.opBoolean","COPY",EDGE,{"disambiguationData":[TD([subQ1])],"derivedFrom":makeQuery(id+"F3.opRevolve","SWEPT_EDGE",EDGE,{"disambiguationData":[OSD([subQ9,subQ4])]})})});}
            var Q123;
            Q123=makeQuery(id+"FENhaPdsYRhXpVq_1.2.F5.boolean.opBoolean","COPY",FACE,{"derivedFrom":makeQuery(id+"FENhaPdsYRhXpVq_1.2.F5.opExtrude","SWEPT_FACE",FACE,{"disambiguationData":[OSD([sQuery(id+"F4.wireOp",EDGE,"E15")])]})});
            var Q124;
            Q124=makeQuery(id+"FENhaPdsYRhXpVq_1.2.F5.boolean.opBoolean","MERGE",FACE,{"derivedFrom":[makeQuery(id+"F3.boolean.opBoolean","COPY",FACE,{"disambiguationData":[TD([makeQuery(id+"F1.opExtrude","SWEPT_FACE",FACE,{"disambiguationData":[OSD([sQuery(id+"F0.wireOp",EDGE,"E7.1.0")])]})])],"derivedFrom":makeQuery(id+"F3.opRevolve","SWEPT_FACE",FACE,{"disambiguationData":[OSD([sQuery(id+"F2.wireOp",EDGE,"E12.bottom")])]})}),makeQuery(id+"FENhaPdsYRhXpVq_1.2.F5.opExtrude","CAP_FACE",FACE,{"disambiguationData":[OSD([sQuery(id+"F4.wireOp",EDGE,"E15")])],"isStart":false})]});
            var Q125;
            {var subQ0=sQuery(id+"F0.wireOp",EDGE,"E9.trimOffspring");var subQ4=sQuery(id+"F0.wireOp",EDGE,"E10.11.3.0");Q125=makeQuery(id+"F3.boolean.opBoolean","SPLIT",EDGE,{"disambiguationData":[TD([makeQuery(id+"F3.opRevolve","SWEPT_FACE",FACE,{"disambiguationData":[OSD([sQuery(id+"F2.wireOp",EDGE,"E12.top")])]})])],"derivedFrom":makeQuery(id+"F1.opExtrude","SWEPT_EDGE",EDGE,{"disambiguationData":[OSD([subQ0,subQ4])]})});}
            var Q126;
            Q126=makeQuery(id+"FENhaPdsYRhXpVq_1.1.F5.boolean.opBoolean","COPY",EDGE,{"derivedFrom":makeQuery(id+"FENhaPdsYRhXpVq_1.1.F5.opExtrude","CAP_EDGE",EDGE,{"disambiguationData":[OSD([sQuery(id+"F4.wireOp",EDGE,"E15")])],"isStart":true})});
            var Q127;
            Q127=makeQuery(id+"F3.boolean.opBoolean","INTERSECT",EDGE,{"derivedFrom":[makeQuery(id+"F1.opExtrude","SWEPT_FACE",FACE,{"disambiguationData":[OSD([sQuery(id+"F0.wireOp",EDGE,"E7.1.3")])]}),makeQuery(id+"F3.opRevolve","SWEPT_FACE",FACE,{"disambiguationData":[OSD([sQuery(id+"F2.wireOp",EDGE,"E12.bottom")])]})]});
            var Q128;
            Q128=makeQuery(id+"F1.opExtrude","CAP_EDGE",EDGE,{"disambiguationData":[OSD([sQuery(id+"F0.wireOp",EDGE,"E8.trimOffspring")])],"isStart":true});
            var Q129;
            Q129=makeQuery(id+"FENhaPdsYRhXpVq_1.3.F5.boolean.opBoolean","COPY",EDGE,{"derivedFrom":makeQuery(id+"FENhaPdsYRhXpVq_1.3.F5.opExtrude","CAP_EDGE",EDGE,{"disambiguationData":[OSD([sQuery(id+"F4.wireOp",EDGE,"E15")])],"isStart":false})});
            var Q130;
            Q130=makeQuery(id+"F1.opExtrude","CAP_EDGE",EDGE,{"disambiguationData":[OSD([sQuery(id+"F0.wireOp",EDGE,"E7.2.2")])],"isStart":true});
            var Q131;
            Q131=makeQuery(id+"F1.opExtrude","CAP_EDGE",EDGE,{"disambiguationData":[OSD([sQuery(id+"F0.wireOp",EDGE,"E5.filletArc")])],"isStart":true});
            var Q132;
            Q132=makeQuery(id+"F1.opExtrude","CAP_EDGE",EDGE,{"disambiguationData":[OSD([sQuery(id+"F0.wireOp",EDGE,"E7.2.3")])],"isStart":true});
            var Q133;
            {var subQ0=sQuery(id+"F0.wireOp",EDGE,"E10.8.3.0");var subQ1=sQuery(id+"F0.wireOp",EDGE,"E10.4.3.0");Q133=makeQuery(id+"F3.boolean.opBoolean","SPLIT",EDGE,{"disambiguationData":[TD([makeQuery(id+"F3.opRevolve","SWEPT_FACE",FACE,{"disambiguationData":[OSD([sQuery(id+"F2.wireOp",EDGE,"E12.bottom")])]})])],"derivedFrom":makeQuery(id+"F1.opExtrude","SWEPT_EDGE",EDGE,{"disambiguationData":[OSD([subQ1,subQ0])]})});}
            var Q134;
            {var subQ2=sQuery(id+"F0.wireOp",EDGE,"E9.trimOffspring");var subQ4=sQuery(id+"F0.wireOp",EDGE,"E10.11.3.0");Q134=makeQuery(id+"F3.boolean.opBoolean","SPLIT",EDGE,{"disambiguationData":[TD([makeQuery(id+"F3.opRevolve","SWEPT_FACE",FACE,{"disambiguationData":[OSD([sQuery(id+"F2.wireOp",EDGE,"E12.bottom")])]})])],"derivedFrom":makeQuery(id+"F1.opExtrude","SWEPT_EDGE",EDGE,{"disambiguationData":[OSD([subQ2,subQ4])]})});}
            var Q135;
            Q135=makeQuery(id+"F3.boolean.opBoolean","INTERSECT",EDGE,{"derivedFrom":[makeQuery(id+"F1.opExtrude","SWEPT_FACE",FACE,{"disambiguationData":[OSD([sQuery(id+"F0.wireOp",EDGE,"E7.1.0")])]}),makeQuery(id+"F3.opRevolve","SWEPT_FACE",FACE,{"disambiguationData":[OSD([sQuery(id+"F2.wireOp",EDGE,"E12.top")])]})]});
            var Q136;
            Q136=makeQuery(id+"F5.boolean.opBoolean","INTERSECT",EDGE,{"disambiguationData":[OD(1.0)],"derivedFrom":[makeQuery(id+"F3.boolean.opBoolean","MERGE",FACE,{"derivedFrom":[makeQuery(id+"F1.opExtrude","SWEPT_FACE",FACE,{"disambiguationData":[OSD([sQuery(id+"F0.wireOp",EDGE,"E1")])]}),makeQuery(id+"F1.opExtrude","SWEPT_FACE",FACE,{"disambiguationData":[OSD([sQuery(id+"F0.wireOp",EDGE,"E8.trimOffspring")])]}),makeQuery(id+"F1.opExtrude","SWEPT_FACE",FACE,{"disambiguationData":[OSD([sQuery(id+"F0.wireOp",EDGE,"E9.trimOffspring")])]}),makeQuery(id+"F1.opExtrude","SWEPT_FACE",FACE,{"disambiguationData":[OSD([sQuery(id+"F0.wireOp",EDGE,"E11.trimOffspring")])]}),makeQuery(id+"F3.opRevolve","SWEPT_FACE",FACE,{"disambiguationData":[OSD([sQuery(id+"F2.wireOp",EDGE,"E12.right")])]})]}),makeQuery(id+"F5.opExtrude","SWEPT_FACE",FACE,{"disambiguationData":[OSD([sQuery(id+"F4.wireOp",EDGE,"E15")])]})]});
            var Q137;
            Q137=makeQuery(id+"F3.boolean.opBoolean","INTERSECT",EDGE,{"derivedFrom":[makeQuery(id+"F1.opExtrude","SWEPT_FACE",FACE,{"disambiguationData":[OSD([sQuery(id+"F0.wireOp",EDGE,"E7.1.2")])]}),makeQuery(id+"F3.opRevolve","SWEPT_FACE",FACE,{"disambiguationData":[OSD([sQuery(id+"F2.wireOp",EDGE,"E12.bottom")])]})]});
            var Q138;
            Q138=makeQuery(id+"F1.opExtrude","CAP_EDGE",EDGE,{"disambiguationData":[OSD([sQuery(id+"F0.wireOp",EDGE,"E2")])],"isStart":true});
            var Q139;
            Q139=makeQuery(id+"FENhaPdsYRhXpVq_1.1.F5.boolean.opBoolean","INTERSECT",EDGE,{"disambiguationData":[OD(1.0)],"derivedFrom":[makeQuery(id+"F3.boolean.opBoolean","MERGE",FACE,{"derivedFrom":[makeQuery(id+"F1.opExtrude","SWEPT_FACE",FACE,{"disambiguationData":[OSD([sQuery(id+"F0.wireOp",EDGE,"E1")])]}),makeQuery(id+"F1.opExtrude","SWEPT_FACE",FACE,{"disambiguationData":[OSD([sQuery(id+"F0.wireOp",EDGE,"E8.trimOffspring")])]}),makeQuery(id+"F1.opExtrude","SWEPT_FACE",FACE,{"disambiguationData":[OSD([sQuery(id+"F0.wireOp",EDGE,"E9.trimOffspring")])]}),makeQuery(id+"F1.opExtrude","SWEPT_FACE",FACE,{"disambiguationData":[OSD([sQuery(id+"F0.wireOp",EDGE,"E11.trimOffspring")])]}),makeQuery(id+"F3.opRevolve","SWEPT_FACE",FACE,{"disambiguationData":[OSD([sQuery(id+"F2.wireOp",EDGE,"E12.right")])]})]}),makeQuery(id+"FENhaPdsYRhXpVq_1.1.F5.opExtrude","SWEPT_FACE",FACE,{"disambiguationData":[OSD([sQuery(id+"F4.wireOp",EDGE,"E15")])]})]});
            var Q140;
            Q140=makeQuery(id+"F3.boolean.opBoolean","INTERSECT",EDGE,{"derivedFrom":[makeQuery(id+"F1.opExtrude","SWEPT_FACE",FACE,{"disambiguationData":[OSD([sQuery(id+"F0.wireOp",EDGE,"E7.2.3")])]}),makeQuery(id+"F3.opRevolve","SWEPT_FACE",FACE,{"disambiguationData":[OSD([sQuery(id+"F2.wireOp",EDGE,"E12.bottom")])]})]});
            var Q141;
            {var subQ0=sQuery(id+"F0.wireOp",EDGE,"E8.trimOffspring");var subQ1=sQuery(id+"F0.wireOp",EDGE,"E7.1.0");Q141=makeQuery(id+"F3.boolean.opBoolean","SPLIT",EDGE,{"disambiguationData":[TD([makeQuery(id+"F3.opRevolve","SWEPT_FACE",FACE,{"disambiguationData":[OSD([sQuery(id+"F2.wireOp",EDGE,"E12.bottom")])]})])],"derivedFrom":makeQuery(id+"F1.opExtrude","SWEPT_EDGE",EDGE,{"disambiguationData":[OSD([subQ1,subQ0])]})});}
            var Q142;
            {var subQ1=sQuery(id+"F0.wireOp",EDGE,"E5.filletArc");var subQ3=sQuery(id+"F0.wireOp",EDGE,"E1");Q142=makeQuery(id+"F3.boolean.opBoolean","SPLIT",EDGE,{"disambiguationData":[TD([makeQuery(id+"F3.opRevolve","SWEPT_FACE",FACE,{"disambiguationData":[OSD([sQuery(id+"F2.wireOp",EDGE,"E12.bottom")])]})])],"derivedFrom":makeQuery(id+"F1.opExtrude","SWEPT_EDGE",EDGE,{"disambiguationData":[OSD([subQ3,subQ1])]})});}
            var Q143;
            Q143=makeQuery(id+"F1.opExtrude","CAP_EDGE",EDGE,{"disambiguationData":[OSD([sQuery(id+"F0.wireOp",EDGE,"E0")])],"isStart":true});
            var Q144;
            Q144=makeQuery(id+"F1.opExtrude","CAP_EDGE",EDGE,{"disambiguationData":[OSD([sQuery(id+"F0.wireOp",EDGE,"E7.1.2")])],"isStart":true});
            var Q145;
            {var subQ0=makeQuery(id+"F1.opExtrude","SWEPT_FACE",FACE,{"disambiguationData":[OSD([sQuery(id+"F0.wireOp",EDGE,"E10.8.3.0")])]});var subQ4=sQuery(id+"F2.wireOp",EDGE,"E12.right");var subQ8=sQuery(id+"F2.wireOp",EDGE,"E12.bottom");Q145=makeQuery(id+"F5.boolean.opBoolean","SPLIT",EDGE,{"disambiguationData":[TD([subQ0])],"derivedFrom":makeQuery(id+"F3.boolean.opBoolean","COPY",EDGE,{"disambiguationData":[TD([subQ0])],"derivedFrom":makeQuery(id+"F3.opRevolve","SWEPT_EDGE",EDGE,{"disambiguationData":[OSD([subQ8,subQ4])]})})});}
            var Q146;
            Q146=makeQuery(id+"FENhaPdsYRhXpVq_1.2.F5.boolean.opBoolean","MERGE",FACE,{"derivedFrom":[makeQuery(id+"F3.boolean.opBoolean","COPY",FACE,{"disambiguationData":[TD([makeQuery(id+"F1.opExtrude","SWEPT_FACE",FACE,{"disambiguationData":[OSD([sQuery(id+"F0.wireOp",EDGE,"E7.1.0")])]})])],"derivedFrom":makeQuery(id+"F3.opRevolve","SWEPT_FACE",FACE,{"disambiguationData":[OSD([sQuery(id+"F2.wireOp",EDGE,"E12.top")])]})}),makeQuery(id+"FENhaPdsYRhXpVq_1.2.F5.opExtrude","CAP_FACE",FACE,{"disambiguationData":[OSD([sQuery(id+"F4.wireOp",EDGE,"E15")])],"isStart":true})]});
            var Q147;
            {var subQ1=sQuery(id+"F0.wireOp",EDGE,"E7.1.1");Q147=makeQuery(id+"F3.boolean.opBoolean","SPLIT",FACE,{"disambiguationData":[TD([makeQuery(id+"F3.opRevolve","SWEPT_FACE",FACE,{"disambiguationData":[OSD([sQuery(id+"F2.wireOp",EDGE,"E12.top")])]})])],"derivedFrom":makeQuery(id+"F1.opExtrude","SWEPT_FACE",FACE,{"disambiguationData":[OSD([subQ1])]})});}
            var Q148;
            {var subQ1=sQuery(id+"F0.wireOp",EDGE,"E7.1.2");var subQ2=sQuery(id+"F0.wireOp",EDGE,"E1");Q148=makeQuery(id+"F3.boolean.opBoolean","SPLIT",EDGE,{"disambiguationData":[TD([makeQuery(id+"F3.opRevolve","SWEPT_FACE",FACE,{"disambiguationData":[OSD([sQuery(id+"F2.wireOp",EDGE,"E12.bottom")])]})])],"derivedFrom":makeQuery(id+"F1.opExtrude","SWEPT_EDGE",EDGE,{"disambiguationData":[OSD([subQ2,subQ1])]})});}
            var Q149;
            Q149=makeQuery(id+"F1.opExtrude","CAP_EDGE",EDGE,{"disambiguationData":[OSD([sQuery(id+"F0.wireOp",EDGE,"E7.1.1")])],"isStart":true});
            var Q150;
            {var subQ0=sQuery(id+"F0.wireOp",EDGE,"E5.filletArc");var subQ1=sQuery(id+"F0.wireOp",EDGE,"E4");Q150=makeQuery(id+"F3.boolean.opBoolean","SPLIT",EDGE,{"disambiguationData":[TD([makeQuery(id+"F3.opRevolve","SWEPT_FACE",FACE,{"disambiguationData":[OSD([sQuery(id+"F2.wireOp",EDGE,"E12.bottom")])]})])],"derivedFrom":makeQuery(id+"F1.opExtrude","SWEPT_EDGE",EDGE,{"disambiguationData":[OSD([subQ1,subQ0])]})});}
            var Q151;
            Q151=makeQuery(id+"FENhaPdsYRhXpVq_1.3.F5.boolean.opBoolean","COPY",EDGE,{"derivedFrom":makeQuery(id+"FENhaPdsYRhXpVq_1.3.F5.opExtrude","CAP_EDGE",EDGE,{"disambiguationData":[OSD([sQuery(id+"F4.wireOp",EDGE,"E15")])],"isStart":true})});
            var Q152;
            {var subQ2=makeQuery(id+"F1.opExtrude","SWEPT_FACE",FACE,{"disambiguationData":[OSD([sQuery(id+"F0.wireOp",EDGE,"E7.1.0")])]});var subQ4=sQuery(id+"F2.wireOp",EDGE,"E12.right");var subQ9=sQuery(id+"F2.wireOp",EDGE,"E12.top");Q152=makeQuery(id+"FENhaPdsYRhXpVq_1.2.F5.boolean.opBoolean","SPLIT",EDGE,{"disambiguationData":[TD([subQ2])],"derivedFrom":makeQuery(id+"F3.boolean.opBoolean","COPY",EDGE,{"disambiguationData":[TD([subQ2])],"derivedFrom":makeQuery(id+"F3.opRevolve","SWEPT_EDGE",EDGE,{"disambiguationData":[OSD([subQ9,subQ4])]})})});}
            var Q153;
            {var subQ0=sQuery(id+"F0.wireOp",EDGE,"E6.filletArc");var subQ1=sQuery(id+"F0.wireOp",EDGE,"E4");Q153=makeQuery(id+"F3.boolean.opBoolean","SPLIT",EDGE,{"disambiguationData":[TD([makeQuery(id+"F3.opRevolve","SWEPT_FACE",FACE,{"disambiguationData":[OSD([sQuery(id+"F2.wireOp",EDGE,"E12.top")])]})])],"derivedFrom":makeQuery(id+"F1.opExtrude","SWEPT_EDGE",EDGE,{"disambiguationData":[OSD([subQ1,subQ0])]})});}
            var Q154;
            {var subQ0=sQuery(id+"F0.wireOp",EDGE,"E10.11.3.0");var subQ1=sQuery(id+"F0.wireOp",EDGE,"E10.4.3.0");Q154=makeQuery(id+"F3.boolean.opBoolean","SPLIT",EDGE,{"disambiguationData":[TD([makeQuery(id+"F3.opRevolve","SWEPT_FACE",FACE,{"disambiguationData":[OSD([sQuery(id+"F2.wireOp",EDGE,"E12.bottom")])]})])],"derivedFrom":makeQuery(id+"F1.opExtrude","SWEPT_EDGE",EDGE,{"disambiguationData":[OSD([subQ1,subQ0])]})});}
            var Q155;
            {var subQ0=sQuery(id+"F0.wireOp",EDGE,"E6.filletArc");var subQ1=sQuery(id+"F0.wireOp",EDGE,"E4");Q155=makeQuery(id+"F3.boolean.opBoolean","SPLIT",EDGE,{"disambiguationData":[TD([makeQuery(id+"F3.opRevolve","SWEPT_FACE",FACE,{"disambiguationData":[OSD([sQuery(id+"F2.wireOp",EDGE,"E12.bottom")])]})])],"derivedFrom":makeQuery(id+"F1.opExtrude","SWEPT_EDGE",EDGE,{"disambiguationData":[OSD([subQ1,subQ0])]})});}
            var Q156;
            {var subQ5=sQuery(id+"F0.wireOp",EDGE,"E7.1.2");Q156=makeQuery(id+"F3.boolean.opBoolean","SPLIT",FACE,{"disambiguationData":[TD([makeQuery(id+"F3.opRevolve","SWEPT_FACE",FACE,{"disambiguationData":[OSD([sQuery(id+"F2.wireOp",EDGE,"E12.top")])]})])],"derivedFrom":makeQuery(id+"F1.opExtrude","SWEPT_FACE",FACE,{"disambiguationData":[OSD([subQ5])]})});}
            var Q157;
            {var subQ0=sQuery(id+"F0.wireOp",EDGE,"E7.2.2");var subQ1=sQuery(id+"F0.wireOp",EDGE,"E7.2.1");Q157=makeQuery(id+"F3.boolean.opBoolean","SPLIT",EDGE,{"disambiguationData":[TD([makeQuery(id+"F3.opRevolve","SWEPT_FACE",FACE,{"disambiguationData":[OSD([sQuery(id+"F2.wireOp",EDGE,"E12.bottom")])]})])],"derivedFrom":makeQuery(id+"F1.opExtrude","SWEPT_EDGE",EDGE,{"disambiguationData":[OSD([subQ1,subQ0])]})});}
            var Q158;
            {var subQ0=sQuery(id+"F0.wireOp",EDGE,"E7.2.1");var subQ1=sQuery(id+"F0.wireOp",EDGE,"E7.2.0");Q158=makeQuery(id+"F3.boolean.opBoolean","SPLIT",EDGE,{"disambiguationData":[TD([makeQuery(id+"F3.opRevolve","SWEPT_FACE",FACE,{"disambiguationData":[OSD([sQuery(id+"F2.wireOp",EDGE,"E12.bottom")])]})])],"derivedFrom":makeQuery(id+"F1.opExtrude","SWEPT_EDGE",EDGE,{"disambiguationData":[OSD([subQ1,subQ0])]})});}
            var Q159;
            Q159=makeQuery(id+"F3.boolean.opBoolean","INTERSECT",EDGE,{"derivedFrom":[makeQuery(id+"F1.opExtrude","SWEPT_FACE",FACE,{"disambiguationData":[OSD([sQuery(id+"F0.wireOp",EDGE,"E7.1.2")])]}),makeQuery(id+"F3.opRevolve","SWEPT_FACE",FACE,{"disambiguationData":[OSD([sQuery(id+"F2.wireOp",EDGE,"E12.top")])]})]});
            var Q160;
            {var subQ5=sQuery(id+"F0.wireOp",EDGE,"E7.2.2");Q160=makeQuery(id+"F3.boolean.opBoolean","SPLIT",FACE,{"disambiguationData":[TD([makeQuery(id+"F3.opRevolve","SWEPT_FACE",FACE,{"disambiguationData":[OSD([sQuery(id+"F2.wireOp",EDGE,"E12.top")])]})])],"derivedFrom":makeQuery(id+"F1.opExtrude","SWEPT_FACE",FACE,{"disambiguationData":[OSD([subQ5])]})});}
            var Q161;
            {var subQ0=sQuery(id+"F0.wireOp",EDGE,"E7.1.3");Q161=makeQuery(id+"F3.boolean.opBoolean","SPLIT",FACE,{"disambiguationData":[TD([makeQuery(id+"F3.opRevolve","SWEPT_FACE",FACE,{"disambiguationData":[OSD([sQuery(id+"F2.wireOp",EDGE,"E12.top")])]})])],"derivedFrom":makeQuery(id+"F1.opExtrude","SWEPT_FACE",FACE,{"disambiguationData":[OSD([subQ0])]})});}
            var Q162;
            Q162=makeQuery(id+"FENhaPdsYRhXpVq_1.2.F5.boolean.opBoolean","COPY",EDGE,{"derivedFrom":makeQuery(id+"FENhaPdsYRhXpVq_1.2.F5.opExtrude","CAP_EDGE",EDGE,{"disambiguationData":[OSD([sQuery(id+"F4.wireOp",EDGE,"E15")])],"isStart":false})});
            var Q163;
            Q163=makeQuery(id+"FENhaPdsYRhXpVq_1.1.F5.boolean.opBoolean","COPY",EDGE,{"derivedFrom":makeQuery(id+"FENhaPdsYRhXpVq_1.1.F5.opExtrude","CAP_EDGE",EDGE,{"disambiguationData":[OSD([sQuery(id+"F4.wireOp",EDGE,"E15")])],"isStart":false})});
            var Q164;
            {var subQ2=makeQuery(id+"F1.opExtrude","SWEPT_FACE",FACE,{"disambiguationData":[OSD([sQuery(id+"F0.wireOp",EDGE,"E7.1.0")])]});var subQ4=sQuery(id+"F2.wireOp",EDGE,"E12.right");var subQ8=sQuery(id+"F2.wireOp",EDGE,"E12.bottom");Q164=makeQuery(id+"FENhaPdsYRhXpVq_1.2.F5.boolean.opBoolean","SPLIT",EDGE,{"disambiguationData":[TD([subQ2])],"derivedFrom":makeQuery(id+"F3.boolean.opBoolean","COPY",EDGE,{"disambiguationData":[TD([subQ2])],"derivedFrom":makeQuery(id+"F3.opRevolve","SWEPT_EDGE",EDGE,{"disambiguationData":[OSD([subQ8,subQ4])]})})});}
            var Q165;
            Q165=makeQuery(id+"F3.boolean.opBoolean","INTERSECT",EDGE,{"derivedFrom":[makeQuery(id+"F1.opExtrude","SWEPT_FACE",FACE,{"disambiguationData":[OSD([sQuery(id+"F0.wireOp",EDGE,"E7.2.2")])]}),makeQuery(id+"F3.opRevolve","SWEPT_FACE",FACE,{"disambiguationData":[OSD([sQuery(id+"F2.wireOp",EDGE,"E12.bottom")])]})]});
            var Q166;
            Q166=makeQuery(id+"F3.boolean.opBoolean","INTERSECT",EDGE,{"derivedFrom":[makeQuery(id+"F1.opExtrude","SWEPT_FACE",FACE,{"disambiguationData":[OSD([sQuery(id+"F0.wireOp",EDGE,"E7.2.2")])]}),makeQuery(id+"F3.opRevolve","SWEPT_FACE",FACE,{"disambiguationData":[OSD([sQuery(id+"F2.wireOp",EDGE,"E12.top")])]})]});
            var Q167;
            {var subQ1=makeQuery(id+"F1.opExtrude","SWEPT_FACE",FACE,{"disambiguationData":[OSD([sQuery(id+"F0.wireOp",EDGE,"E5.filletArc")])]});var subQ4=sQuery(id+"F2.wireOp",EDGE,"E12.right");var subQ8=sQuery(id+"F2.wireOp",EDGE,"E12.bottom");Q167=makeQuery(id+"FENhaPdsYRhXpVq_1.1.F5.boolean.opBoolean","SPLIT",EDGE,{"disambiguationData":[TD([subQ1])],"derivedFrom":makeQuery(id+"F3.boolean.opBoolean","COPY",EDGE,{"disambiguationData":[TD([subQ1])],"derivedFrom":makeQuery(id+"F3.opRevolve","SWEPT_EDGE",EDGE,{"disambiguationData":[OSD([subQ8,subQ4])]})})});}
            var Q168;
            {var subQ2=makeQuery(id+"F1.opExtrude","SWEPT_FACE",FACE,{"disambiguationData":[OSD([sQuery(id+"F0.wireOp",EDGE,"E7.1.2")])]});var subQ3=makeQuery(id+"F1.opExtrude","SWEPT_FACE",FACE,{"disambiguationData":[OSD([sQuery(id+"F0.wireOp",EDGE,"E7.1.0")])]});var subQ5=sQuery(id+"F2.wireOp",EDGE,"E12.right");var subQ8=sQuery(id+"F2.wireOp",EDGE,"E12.top");Q168=makeQuery(id+"FENhaPdsYRhXpVq_1.2.F5.boolean.opBoolean","SPLIT",EDGE,{"disambiguationData":[TD([subQ2])],"derivedFrom":makeQuery(id+"F3.boolean.opBoolean","COPY",EDGE,{"disambiguationData":[TD([subQ3])],"derivedFrom":makeQuery(id+"F3.opRevolve","SWEPT_EDGE",EDGE,{"disambiguationData":[OSD([subQ8,subQ5])]})})});}
            var Q169;
            {var subQ1=makeQuery(id+"F1.opExtrude","SWEPT_FACE",FACE,{"disambiguationData":[OSD([sQuery(id+"F0.wireOp",EDGE,"E7.1.2")])]});var subQ2=makeQuery(id+"F1.opExtrude","SWEPT_FACE",FACE,{"disambiguationData":[OSD([sQuery(id+"F0.wireOp",EDGE,"E7.1.0")])]});var subQ4=sQuery(id+"F2.wireOp",EDGE,"E12.right");var subQ8=sQuery(id+"F2.wireOp",EDGE,"E12.bottom");Q169=makeQuery(id+"FENhaPdsYRhXpVq_1.2.F5.boolean.opBoolean","SPLIT",EDGE,{"disambiguationData":[TD([subQ1])],"derivedFrom":makeQuery(id+"F3.boolean.opBoolean","COPY",EDGE,{"disambiguationData":[TD([subQ2])],"derivedFrom":makeQuery(id+"F3.opRevolve","SWEPT_EDGE",EDGE,{"disambiguationData":[OSD([subQ8,subQ4])]})})});}
            var Q170;
            Q170=makeQuery(id+"FENhaPdsYRhXpVq_1.2.F5.boolean.opBoolean","COPY",EDGE,{"derivedFrom":makeQuery(id+"FENhaPdsYRhXpVq_1.2.F5.opExtrude","CAP_EDGE",EDGE,{"disambiguationData":[OSD([sQuery(id+"F4.wireOp",EDGE,"E15")])],"isStart":true})});
            var Q171;
            Q171=makeQuery(id+"F3.boolean.opBoolean","INTERSECT",EDGE,{"derivedFrom":[makeQuery(id+"F1.opExtrude","SWEPT_FACE",FACE,{"disambiguationData":[OSD([sQuery(id+"F0.wireOp",EDGE,"E7.1.0")])]}),makeQuery(id+"F3.opRevolve","SWEPT_FACE",FACE,{"disambiguationData":[OSD([sQuery(id+"F2.wireOp",EDGE,"E12.bottom")])]})]});
            var Q172;
            {var subQ2=makeQuery(id+"F1.opExtrude","SWEPT_FACE",FACE,{"disambiguationData":[OSD([sQuery(id+"F0.wireOp",EDGE,"E7.2.2")])]});var subQ4=sQuery(id+"F2.wireOp",EDGE,"E12.right");var subQ7=makeQuery(id+"F1.opExtrude","SWEPT_FACE",FACE,{"disambiguationData":[OSD([sQuery(id+"F0.wireOp",EDGE,"E7.2.0")])]});var subQ8=sQuery(id+"F2.wireOp",EDGE,"E12.top");Q172=makeQuery(id+"FENhaPdsYRhXpVq_1.3.F5.boolean.opBoolean","SPLIT",EDGE,{"disambiguationData":[TD([subQ2])],"derivedFrom":makeQuery(id+"F3.boolean.opBoolean","COPY",EDGE,{"disambiguationData":[TD([subQ7])],"derivedFrom":makeQuery(id+"F3.opRevolve","SWEPT_EDGE",EDGE,{"disambiguationData":[OSD([subQ8,subQ4])]})})});}
            var Q173;
            Q173=makeQuery(id+"F3.boolean.opBoolean","INTERSECT",EDGE,{"derivedFrom":[makeQuery(id+"F1.opExtrude","SWEPT_FACE",FACE,{"disambiguationData":[OSD([sQuery(id+"F0.wireOp",EDGE,"E7.1.1")])]}),makeQuery(id+"F3.opRevolve","SWEPT_FACE",FACE,{"disambiguationData":[OSD([sQuery(id+"F2.wireOp",EDGE,"E12.bottom")])]})]});
            var Q174;
            {var subQ0=sQuery(id+"F0.wireOp",EDGE,"E7.1.2");var subQ1=sQuery(id+"F0.wireOp",EDGE,"E7.1.1");Q174=makeQuery(id+"F3.boolean.opBoolean","SPLIT",EDGE,{"disambiguationData":[TD([makeQuery(id+"F3.opRevolve","SWEPT_FACE",FACE,{"disambiguationData":[OSD([sQuery(id+"F2.wireOp",EDGE,"E12.bottom")])]})])],"derivedFrom":makeQuery(id+"F1.opExtrude","SWEPT_EDGE",EDGE,{"disambiguationData":[OSD([subQ1,subQ0])]})});}
            var Q175;
            {var subQ0=sQuery(id+"F0.wireOp",EDGE,"E7.2.1");var subQ1=sQuery(id+"F0.wireOp",EDGE,"E7.2.0");Q175=makeQuery(id+"F3.boolean.opBoolean","SPLIT",EDGE,{"disambiguationData":[TD([makeQuery(id+"F3.opRevolve","SWEPT_FACE",FACE,{"disambiguationData":[OSD([sQuery(id+"F2.wireOp",EDGE,"E12.top")])]})])],"derivedFrom":makeQuery(id+"F1.opExtrude","SWEPT_EDGE",EDGE,{"disambiguationData":[OSD([subQ1,subQ0])]})});}
            var Q176;
            {var subQ0=sQuery(id+"F0.wireOp",EDGE,"E7.2.0");var subQ1=sQuery(id+"F0.wireOp",EDGE,"E11.trimOffspring");Q176=makeQuery(id+"F3.boolean.opBoolean","SPLIT",EDGE,{"disambiguationData":[TD([makeQuery(id+"F3.opRevolve","SWEPT_FACE",FACE,{"disambiguationData":[OSD([sQuery(id+"F2.wireOp",EDGE,"E12.top")])]})])],"derivedFrom":makeQuery(id+"F1.opExtrude","SWEPT_EDGE",EDGE,{"disambiguationData":[OSD([subQ0,subQ1])]})});}
            var Q177;
            {var subQ0=makeQuery(id+"F1.opExtrude","SWEPT_FACE",FACE,{"disambiguationData":[OSD([sQuery(id+"F0.wireOp",EDGE,"E10.11.3.0")])]});var subQ5=sQuery(id+"F2.wireOp",EDGE,"E12.right");var subQ8=makeQuery(id+"F1.opExtrude","SWEPT_FACE",FACE,{"disambiguationData":[OSD([sQuery(id+"F0.wireOp",EDGE,"E10.8.3.0")])]});var subQ9=sQuery(id+"F2.wireOp",EDGE,"E12.top");Q177=makeQuery(id+"F5.boolean.opBoolean","SPLIT",EDGE,{"disambiguationData":[TD([subQ0])],"derivedFrom":makeQuery(id+"F3.boolean.opBoolean","COPY",EDGE,{"disambiguationData":[TD([subQ8])],"derivedFrom":makeQuery(id+"F3.opRevolve","SWEPT_EDGE",EDGE,{"disambiguationData":[OSD([subQ9,subQ5])]})})});}
            var Q178;
            {var subQ0=sQuery(id+"F0.wireOp",EDGE,"E7.1.0");var subQ2=sQuery(id+"F0.wireOp",EDGE,"E8.trimOffspring");Q178=makeQuery(id+"F3.boolean.opBoolean","SPLIT",EDGE,{"disambiguationData":[TD([makeQuery(id+"F3.opRevolve","SWEPT_FACE",FACE,{"disambiguationData":[OSD([sQuery(id+"F2.wireOp",EDGE,"E12.top")])]})])],"derivedFrom":makeQuery(id+"F1.opExtrude","SWEPT_EDGE",EDGE,{"disambiguationData":[OSD([subQ0,subQ2])]})});}
            var Q179;
            Q179=makeQuery(id+"F3.boolean.opBoolean","INTERSECT",EDGE,{"derivedFrom":[makeQuery(id+"F1.opExtrude","SWEPT_FACE",FACE,{"disambiguationData":[OSD([sQuery(id+"F0.wireOp",EDGE,"E7.1.3")])]}),makeQuery(id+"F3.opRevolve","SWEPT_FACE",FACE,{"disambiguationData":[OSD([sQuery(id+"F2.wireOp",EDGE,"E12.top")])]})]});
            var Q180;
            {var subQ0=sQuery(id+"F0.wireOp",EDGE,"E7.1.2");var subQ1=sQuery(id+"F0.wireOp",EDGE,"E1");Q180=makeQuery(id+"F3.boolean.opBoolean","SPLIT",EDGE,{"disambiguationData":[TD([makeQuery(id+"F3.opRevolve","SWEPT_FACE",FACE,{"disambiguationData":[OSD([sQuery(id+"F2.wireOp",EDGE,"E12.top")])]})])],"derivedFrom":makeQuery(id+"F1.opExtrude","SWEPT_EDGE",EDGE,{"disambiguationData":[OSD([subQ1,subQ0])]})});}
            var Q181;
            {var subQ0=sQuery(id+"F0.wireOp",EDGE,"E7.1.1");var subQ1=sQuery(id+"F0.wireOp",EDGE,"E7.1.0");Q181=makeQuery(id+"F3.boolean.opBoolean","SPLIT",EDGE,{"disambiguationData":[TD([makeQuery(id+"F3.opRevolve","SWEPT_FACE",FACE,{"disambiguationData":[OSD([sQuery(id+"F2.wireOp",EDGE,"E12.top")])]})])],"derivedFrom":makeQuery(id+"F1.opExtrude","SWEPT_EDGE",EDGE,{"disambiguationData":[OSD([subQ1,subQ0])]})});}
            var Q182;
            {var subQ0=sQuery(id+"F0.wireOp",EDGE,"E7.2.2");var subQ2=sQuery(id+"F0.wireOp",EDGE,"E8.trimOffspring");Q182=makeQuery(id+"F3.boolean.opBoolean","SPLIT",EDGE,{"disambiguationData":[TD([makeQuery(id+"F3.opRevolve","SWEPT_FACE",FACE,{"disambiguationData":[OSD([sQuery(id+"F2.wireOp",EDGE,"E12.top")])]})])],"derivedFrom":makeQuery(id+"F1.opExtrude","SWEPT_EDGE",EDGE,{"disambiguationData":[OSD([subQ0,subQ2])]})});}
            var Q183;
            {var subQ0=sQuery(id+"F4.wireOp",EDGE,"E15");var subQ5=sQuery(id+"F0.wireOp",EDGE,"E7.1.0");var subQ6=makeQuery(id+"F1.opExtrude","SWEPT_FACE",FACE,{"disambiguationData":[OSD([subQ5])]});var subQ7=sQuery(id+"F0.wireOp",EDGE,"E1");var subQ8=makeQuery(id+"F1.opExtrude","SWEPT_FACE",FACE,{"disambiguationData":[OSD([subQ7])]});var subQ9=makeQuery(id+"F3.opRevolve","SWEPT_FACE",FACE,{"disambiguationData":[OSD([sQuery(id+"F2.wireOp",EDGE,"E12.right")])]});var subQ12=sQuery(id+"F0.wireOp",EDGE,"E11.trimOffspring");var subQ13=makeQuery(id+"F1.opExtrude","SWEPT_FACE",FACE,{"disambiguationData":[OSD([subQ12])]});var subQ14=sQuery(id+"F0.wireOp",EDGE,"E8.trimOffspring");var subQ15=makeQuery(id+"F1.opExtrude","SWEPT_FACE",FACE,{"disambiguationData":[OSD([subQ14])]});var subQ16=sQuery(id+"F0.wireOp",EDGE,"E9.trimOffspring");var subQ17=makeQuery(id+"F1.opExtrude","SWEPT_FACE",FACE,{"disambiguationData":[OSD([subQ16])]});var subQ36=sQuery(id+"F0.wireOp",EDGE,"E5.filletArc");var subQ52=makeQuery(id+"F1.opExtrude","SWEPT_FACE",FACE,{"disambiguationData":[OSD([subQ36])]});Q183=makeQuery(id+"FENhaPdsYRhXpVq_1.3.F5.boolean.opBoolean","INTERSECT",EDGE,{"disambiguationData":[OD(1.0)],"derivedFrom":[makeQuery(id+"FENhaPdsYRhXpVq_1.2.F5.boolean.opBoolean","SPLIT",FACE,{"disambiguationData":[TD([subQ6])],"derivedFrom":makeQuery(id+"FENhaPdsYRhXpVq_1.1.F5.boolean.opBoolean","SPLIT",FACE,{"disambiguationData":[TD([subQ52])],"derivedFrom":makeQuery(id+"F3.boolean.opBoolean","MERGE",FACE,{"derivedFrom":[subQ8,subQ15,subQ17,subQ13,subQ9]})})}),makeQuery(id+"FENhaPdsYRhXpVq_1.3.F5.opExtrude","SWEPT_FACE",FACE,{"disambiguationData":[OSD([subQ0])]})]});}
            var Q184;
            {var subQ0=sQuery(id+"F0.wireOp",EDGE,"E7.2.2");var subQ1=sQuery(id+"F0.wireOp",EDGE,"E7.2.1");Q184=makeQuery(id+"F3.boolean.opBoolean","SPLIT",EDGE,{"disambiguationData":[TD([makeQuery(id+"F3.opRevolve","SWEPT_FACE",FACE,{"disambiguationData":[OSD([sQuery(id+"F2.wireOp",EDGE,"E12.top")])]})])],"derivedFrom":makeQuery(id+"F1.opExtrude","SWEPT_EDGE",EDGE,{"disambiguationData":[OSD([subQ1,subQ0])]})});}
            var Q185;
            {var subQ0=sQuery(id+"F4.wireOp",EDGE,"E15");var subQ1=sQuery(id+"F0.wireOp",EDGE,"E5.filletArc");var subQ2=makeQuery(id+"F1.opExtrude","SWEPT_FACE",FACE,{"disambiguationData":[OSD([subQ1])]});var subQ3=sQuery(id+"F0.wireOp",EDGE,"E9.trimOffspring");var subQ4=makeQuery(id+"F1.opExtrude","SWEPT_FACE",FACE,{"disambiguationData":[OSD([subQ3])]});var subQ7=sQuery(id+"F0.wireOp",EDGE,"E8.trimOffspring");var subQ8=makeQuery(id+"F1.opExtrude","SWEPT_FACE",FACE,{"disambiguationData":[OSD([subQ7])]});var subQ11=sQuery(id+"F0.wireOp",EDGE,"E1");var subQ12=makeQuery(id+"F1.opExtrude","SWEPT_FACE",FACE,{"disambiguationData":[OSD([subQ11])]});var subQ13=makeQuery(id+"F3.opRevolve","SWEPT_FACE",FACE,{"disambiguationData":[OSD([sQuery(id+"F2.wireOp",EDGE,"E12.right")])]});var subQ16=sQuery(id+"F0.wireOp",EDGE,"E11.trimOffspring");var subQ17=makeQuery(id+"F1.opExtrude","SWEPT_FACE",FACE,{"disambiguationData":[OSD([subQ16])]});Q185=makeQuery(id+"FENhaPdsYRhXpVq_1.2.F5.boolean.opBoolean","INTERSECT",EDGE,{"disambiguationData":[OD(0.0)],"derivedFrom":[makeQuery(id+"FENhaPdsYRhXpVq_1.1.F5.boolean.opBoolean","SPLIT",FACE,{"disambiguationData":[TD([subQ2])],"derivedFrom":makeQuery(id+"F3.boolean.opBoolean","MERGE",FACE,{"derivedFrom":[subQ12,subQ8,subQ4,subQ17,subQ13]})}),makeQuery(id+"FENhaPdsYRhXpVq_1.2.F5.opExtrude","SWEPT_FACE",FACE,{"disambiguationData":[OSD([subQ0])]})]});}
            var Q186;
            {var subQ0=sQuery(id+"F4.wireOp",EDGE,"E15");var subQ1=sQuery(id+"F0.wireOp",EDGE,"E5.filletArc");var subQ2=makeQuery(id+"F1.opExtrude","SWEPT_FACE",FACE,{"disambiguationData":[OSD([subQ1])]});var subQ3=sQuery(id+"F0.wireOp",EDGE,"E9.trimOffspring");var subQ4=makeQuery(id+"F1.opExtrude","SWEPT_FACE",FACE,{"disambiguationData":[OSD([subQ3])]});var subQ7=sQuery(id+"F0.wireOp",EDGE,"E8.trimOffspring");var subQ8=makeQuery(id+"F1.opExtrude","SWEPT_FACE",FACE,{"disambiguationData":[OSD([subQ7])]});var subQ11=sQuery(id+"F0.wireOp",EDGE,"E1");var subQ12=makeQuery(id+"F1.opExtrude","SWEPT_FACE",FACE,{"disambiguationData":[OSD([subQ11])]});var subQ13=makeQuery(id+"F3.opRevolve","SWEPT_FACE",FACE,{"disambiguationData":[OSD([sQuery(id+"F2.wireOp",EDGE,"E12.right")])]});var subQ16=sQuery(id+"F0.wireOp",EDGE,"E11.trimOffspring");var subQ17=makeQuery(id+"F1.opExtrude","SWEPT_FACE",FACE,{"disambiguationData":[OSD([subQ16])]});Q186=makeQuery(id+"FENhaPdsYRhXpVq_1.2.F5.boolean.opBoolean","INTERSECT",EDGE,{"disambiguationData":[OD(1.0)],"derivedFrom":[makeQuery(id+"FENhaPdsYRhXpVq_1.1.F5.boolean.opBoolean","SPLIT",FACE,{"disambiguationData":[TD([subQ2])],"derivedFrom":makeQuery(id+"F3.boolean.opBoolean","MERGE",FACE,{"derivedFrom":[subQ12,subQ8,subQ4,subQ17,subQ13]})}),makeQuery(id+"FENhaPdsYRhXpVq_1.2.F5.opExtrude","SWEPT_FACE",FACE,{"disambiguationData":[OSD([subQ0])]})]});}
            var Q187;
            {var subQ0=sQuery(id+"F4.wireOp",EDGE,"E15");var subQ5=sQuery(id+"F0.wireOp",EDGE,"E7.1.0");var subQ6=makeQuery(id+"F1.opExtrude","SWEPT_FACE",FACE,{"disambiguationData":[OSD([subQ5])]});var subQ7=sQuery(id+"F0.wireOp",EDGE,"E1");var subQ8=makeQuery(id+"F1.opExtrude","SWEPT_FACE",FACE,{"disambiguationData":[OSD([subQ7])]});var subQ9=makeQuery(id+"F3.opRevolve","SWEPT_FACE",FACE,{"disambiguationData":[OSD([sQuery(id+"F2.wireOp",EDGE,"E12.right")])]});var subQ12=sQuery(id+"F0.wireOp",EDGE,"E11.trimOffspring");var subQ13=makeQuery(id+"F1.opExtrude","SWEPT_FACE",FACE,{"disambiguationData":[OSD([subQ12])]});var subQ14=sQuery(id+"F0.wireOp",EDGE,"E8.trimOffspring");var subQ15=makeQuery(id+"F1.opExtrude","SWEPT_FACE",FACE,{"disambiguationData":[OSD([subQ14])]});var subQ16=sQuery(id+"F0.wireOp",EDGE,"E9.trimOffspring");var subQ17=makeQuery(id+"F1.opExtrude","SWEPT_FACE",FACE,{"disambiguationData":[OSD([subQ16])]});var subQ36=sQuery(id+"F0.wireOp",EDGE,"E5.filletArc");var subQ52=makeQuery(id+"F1.opExtrude","SWEPT_FACE",FACE,{"disambiguationData":[OSD([subQ36])]});Q187=makeQuery(id+"FENhaPdsYRhXpVq_1.3.F5.boolean.opBoolean","INTERSECT",EDGE,{"disambiguationData":[OD(0.0)],"derivedFrom":[makeQuery(id+"FENhaPdsYRhXpVq_1.2.F5.boolean.opBoolean","SPLIT",FACE,{"disambiguationData":[TD([subQ6])],"derivedFrom":makeQuery(id+"FENhaPdsYRhXpVq_1.1.F5.boolean.opBoolean","SPLIT",FACE,{"disambiguationData":[TD([subQ52])],"derivedFrom":makeQuery(id+"F3.boolean.opBoolean","MERGE",FACE,{"derivedFrom":[subQ8,subQ15,subQ17,subQ13,subQ9]})})}),makeQuery(id+"FENhaPdsYRhXpVq_1.3.F5.opExtrude","SWEPT_FACE",FACE,{"disambiguationData":[OSD([subQ0])]})]});}
            var Q188;
            {var subQ0=sQuery(id+"F0.wireOp",EDGE,"E7.1.2");var subQ1=sQuery(id+"F0.wireOp",EDGE,"E7.1.1");Q188=makeQuery(id+"F3.boolean.opBoolean","SPLIT",EDGE,{"disambiguationData":[TD([makeQuery(id+"F3.opRevolve","SWEPT_FACE",FACE,{"disambiguationData":[OSD([sQuery(id+"F2.wireOp",EDGE,"E12.top")])]})])],"derivedFrom":makeQuery(id+"F1.opExtrude","SWEPT_EDGE",EDGE,{"disambiguationData":[OSD([subQ1,subQ0])]})});}
            var Q189;
            Q189=makeQuery(id+"F7.boolean.opBoolean","COPY",FACE,{"derivedFrom":makeQuery(id+"F7.opExtrude","CAP_FACE",FACE,{"disambiguationData":[OSD([sQuery(id+"F6.wireOp",EDGE,"E16"),sQuery(id+"F6.wireOp",EDGE,"E17.1.0"),sQuery(id+"F6.wireOp",EDGE,"E17.2.0"),sQuery(id+"F6.wireOp",EDGE,"E17.3.0"),sQuery(id+"F6.wireOp",EDGE,"E18")])],"isStart":false})});
            fillet(context, id + "F10", {"entities" : qUnion([Q0, Q1, Q2, Q3, Q4, Q5, Q6, Q7, Q8, Q9, Q10, Q11, Q12, Q13, Q14, Q15, Q16, Q17, Q18, Q19, Q20, Q21, Q22, Q23, Q24, Q25, Q26, Q27, Q28, Q29, Q30, Q31, Q32, Q33, Q34, Q35, Q36, Q37, Q38, Q39, Q40, Q41, Q42, Q43, Q44, Q45, Q46, Q47, Q48, Q49, Q50, Q51, Q52, Q53, Q54, Q55, Q56, Q57, Q58, Q59, Q60, Q61, Q62, Q63, Q64, Q65, Q66, Q67, Q68, Q69, Q70, Q71, Q72, Q73, Q74, Q75, Q76, Q77, Q78, Q79, Q80, Q81, Q82, Q83, Q84, Q85, Q86, Q87, Q88, Q89, Q90, Q91, Q92, Q93, Q94, Q95, Q96, Q97, Q98, Q99, Q100, Q101, Q102, Q103, Q104, Q105, Q106, Q107, Q108, Q109, Q110, Q111, Q112, Q113, Q114, Q115, Q116, Q117, Q118, Q119, Q120, Q121, Q122, Q123, Q124, Q125, Q126, Q127, Q128, Q129, Q130, Q131, Q132, Q133, Q134, Q135, Q136, Q137, Q138, Q139, Q140, Q141, Q142, Q143, Q144, Q145, Q146, Q147, Q148, Q149, Q150, Q151, Q152, Q153, Q154, Q155, Q156, Q157, Q158, Q159, Q160, Q161, Q162, Q163, Q164, Q165, Q166, Q167, Q168, Q169, Q170, Q171, Q172, Q173, Q174, Q175, Q176, Q177, Q178, Q179, Q180, Q181, Q182, Q183, Q184, Q185, Q186, Q187, Q188, Q189]), "radius" : 0.25 * mm, "tangentPropagation" : true, "allowEdgeOverflow" : false});
        }
    });
